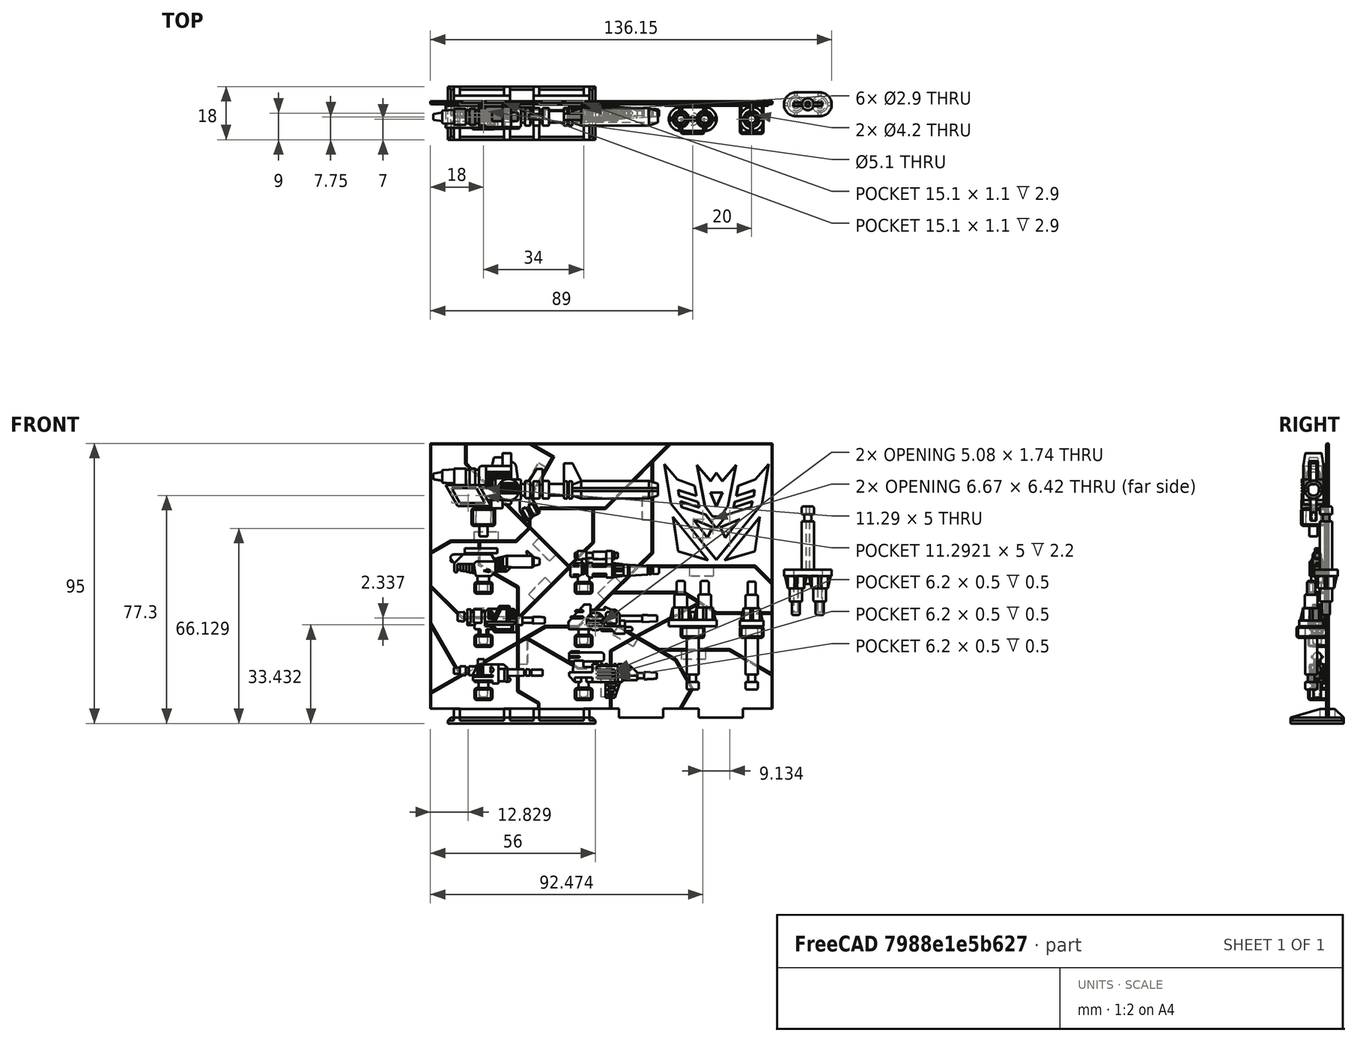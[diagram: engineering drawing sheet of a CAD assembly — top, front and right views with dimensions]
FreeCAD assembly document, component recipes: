
FREECAD ASSEMBLY — COMPONENT RECIPES ("Accesories")

This assembly document has 10 components, labeled P0..P9 below (a component is one placed body or linked part). 9 of them carry a construction recipe — the FreeCAD feature program that regenerates the part from scratch, quoted from this document or its linked companion documents; the rest are supplied as boundary geometry only. No exploded tour is included for this assembly.
NOTE — document 2 of 3 of this assembly tour. The two overview renders and the header above are repeated from document 1; the component sections below continue where the previous document stopped.
COMPONENT P4 — recipe-attached ("Scrapper_Gun", modeled in this document).
Construction recipe (the document's own serialized feature program — sketch geometry with constraints, then the solid features built on it; lengths are millimeters unless a unit is written):

FEATURE [Sketcher::SketchObject] Sketch283
  ArcFitTolerance = 1e-06
  AttachmentSupport = -> [XZ_Plane023]
  FullyConstrained = true
  MakeInternals = false
  MapMode = 5
  Placement = pos=(0,0,0) rot=(1,0,0;1.5708rad)
  sketch-geometry (15):
    g0: LineSegment StartX=0 StartY=0 StartZ=0 EndX=14.5 EndY=0 EndZ=0
    g1: LineSegment StartX=14.5 StartY=0 StartZ=0 EndX=16 EndY=-1.6 EndZ=0
    g2: LineSegment StartX=16 StartY=-1.6 StartZ=0 EndX=19.1 EndY=-1.6 EndZ=0
    g3: LineSegment StartX=19.1 StartY=-1.6 StartZ=0 EndX=19.1 EndY=2.9 EndZ=0
    g4: LineSegment StartX=19.1 StartY=2.9 StartZ=0 EndX=17.3 EndY=2.9 EndZ=0
    g5: LineSegment StartX=17.3 StartY=2.9 StartZ=0 EndX=17.3 EndY=5.2 EndZ=0
    g6: LineSegment StartX=17.3 StartY=5.2 StartZ=0 EndX=15.9 EndY=6.6 EndZ=0
    g7: LineSegment StartX=15.9 StartY=6.6 StartZ=0 EndX=14.4028 EndY=6.6 EndZ=0
    g8: LineSegment StartX=14.4028 StartY=6.6 StartZ=0 EndX=12.1028 EndY=7.6 EndZ=0
    g9: LineSegment StartX=12.1028 StartY=7.6 StartZ=0 EndX=12.1028 EndY=6.6 EndZ=0
    g10: LineSegment StartX=12.1028 StartY=6.6 StartZ=0 EndX=7.40278 EndY=6.6 EndZ=0
    g11: LineSegment StartX=7.40278 StartY=6.6 StartZ=0 EndX=7.40278 EndY=8.4 EndZ=0
    g12: LineSegment StartX=7.40278 StartY=8.4 StartZ=0 EndX=5.40278 EndY=8.4 EndZ=0
    g13: LineSegment StartX=5.40278 StartY=8.4 StartZ=0 EndX=0 EndY=2.5 EndZ=0
    g14: LineSegment StartX=0 StartY=2.5 StartZ=0 EndX=0 EndY=0 EndZ=0
  constraints (44):
    c: Coincident(g0,g-1)
    c: PointOnObject(g0,g-1)
    c: Coincident(g1,g0)
    c: Coincident(g2,g1)
    c: Horizontal(g2)
    c: Coincident(g3,g2)
    c: Vertical(g3)
    c: Coincident(g4,g3)
    c: Horizontal(g4)
    c: Coincident(g5,g4)
    c: Vertical(g5)
    c: Coincident(g6,g5)
    c: Coincident(g7,g6)
    c: Horizontal(g7)
    c: Coincident(g8,g7)
    c: Coincident(g9,g8)
    c: Coincident(g10,g9)
    c: Horizontal(g10)
    c: Coincident(g11,g10)
    c: Vertical(g11)
    c: Coincident(g12,g11)
    c: Horizontal(g12)
    c: Coincident(g13,g12)
    c: Coincident(g14,g13)
    c: Coincident(g14,g0)
    c: Vertical(g14)
    c: DistanceX(g0,g0) = 14.5
    c: DistanceY(g1,g0) = 1.6
    c: DistanceX(g2,g2) = 3.1
    c: DistanceY(g3,g3) = 4.5
    c: DistanceX(g0,g2) = 19.1
    c: DistanceX(g10,g10) = 4.7
    c: DistanceY(g14,g14) = 2.5
    c: DistanceY(g0,g12) = 8.4
    c: DistanceX(g12,g12) = 2
    c: DistanceX(g9,g7) = 2.3
    c: DistanceY(g11,g11) = 1.8
    c: Angle(g7,g6) = 2.35619
    c: DistanceX(g4,g4) = 1.8
    c: DistanceY(g7,g9) = 0
    c: Vertical(g9)
    c: Distance(g13) = 8
    c: DistanceY(g9,g9) = 1
    c: DistanceY(g5,g5) = 2.3
FEATURE [PartDesign::Pad] Pad188
  Direction = (0,-1,2e-16)
  Length = 4.5
  Length2 = 10
  Placement = pos=(0,0,0) rot=(1,0,0;1.5708rad)
  Profile = -> Sketch283
  ReferenceAxis = -> Sketch283 [N_Axis]
  Refine = true
  Suppressed = false
  Type = 0
FEATURE [Sketcher::SketchObject] Sketch284
  ArcFitTolerance = 1e-06
  AttachmentSupport = -> [Pad188]
  ExternalGeometry = -> [Pad188]
  FullyConstrained = true
  MakeInternals = false
  MapMode = 5
  Placement = pos=(0,-4.5,0) rot=(1,0,0;1.5708rad)
  sketch-geometry (1):
    g0: Circle CenterX=9.1 CenterY=2.6 CenterZ=0 NormalX=0 NormalY=0 NormalZ=1 AngleXU=0 Radius=3
  constraints (3):
    c: Diameter(g0) = 6
    c: DistanceX(g-1,g0) = 9.1
    c: DistanceY(g0,g-3) = 4
FEATURE [PartDesign::Pad] Pad189
  BaseFeature = -> Pad188
  Direction = (0,-1,2e-16)
  Length = 0.25
  Length2 = 10
  Placement = pos=(0,0,0) rot=(1,0,0;1.5708rad)
  Profile = -> Sketch284
  ReferenceAxis = -> Sketch284 [N_Axis]
  Refine = true
  Suppressed = false
  Type = 0
FEATURE [PartDesign::Pad] Pad190
  BaseFeature = -> Pad189
  Direction = (0,-1,2e-16)
  Length = 4.75
  Length2 = 10
  Placement = pos=(0,0,0) rot=(1,0,0;1.5708rad)
  Profile = -> Sketch284
  ReferenceAxis = -> Sketch284 [N_Axis]
  Refine = true
  Reversed = true
  Suppressed = false
  Type = 0
FEATURE [Sketcher::SketchObject] Sketch285
  ArcFitTolerance = 1e-06
  AttachmentSupport = -> [Pad190]
  ExternalGeometry = -> [Pad190]
  FullyConstrained = true
  MakeInternals = false
  MapMode = 5
  Placement = pos=(0,-4.5,0) rot=(1,0,0;1.5708rad)
  sketch-geometry (13):
    g0: LineSegment StartX=7.40278 StartY=6.6 StartZ=0 EndX=12.1028 EndY=6.6 EndZ=0
    g1: LineSegment StartX=12.1028 StartY=6.6 StartZ=0 EndX=12.1028 EndY=7.6 EndZ=0
    g2: LineSegment StartX=12.1028 StartY=7.6 StartZ=0 EndX=14.4028 EndY=6.6 EndZ=0
    g3: LineSegment StartX=14.4028 StartY=6.6 StartZ=0 EndX=15.9 EndY=6.6 EndZ=0
    g4: LineSegment StartX=15.9 StartY=6.6 StartZ=0 EndX=17.3 EndY=5.2 EndZ=0
    g5: LineSegment StartX=17.3 StartY=5.2 StartZ=0 EndX=17.3 EndY=2.9 EndZ=0
    g6: LineSegment StartX=17.3 StartY=2.9 StartZ=0 EndX=19.1 EndY=2.9 EndZ=0
    g7: LineSegment StartX=19.1 StartY=2.9 StartZ=0 EndX=19.1 EndY=-1.6 EndZ=0
    g8: LineSegment StartX=19.1 StartY=-1.6 StartZ=0 EndX=16 EndY=-1.6 EndZ=0
    g9: LineSegment StartX=16 StartY=-1.6 StartZ=0 EndX=14.5 EndY=0 EndZ=0
    g10: LineSegment StartX=14.5 StartY=0 StartZ=0 EndX=10.5967 EndY=6.8927e-12 EndZ=0
    g11: LineSegment StartX=7.40278 StartY=6.6 StartZ=0 EndX=7.40278 EndY=5.07375 EndZ=0
    g12: ArcOfCircle CenterX=9.10001 CenterY=2.6 CenterZ=0 NormalX=0 NormalY=0 NormalZ=1 AngleXU=0 Radius=3 StartAngle=5.2347 EndAngle=8.45532
  constraints (28):
    c: Coincident(g0,g-3)
    c: Coincident(g0,g-4)
    c: Coincident(g1,g0)
    c: Coincident(g1,g-5)
    c: Coincident(g2,g1)
    c: Coincident(g2,g-6)
    c: Coincident(g3,g2)
    c: Coincident(g3,g-7)
    c: Coincident(g4,g3)
    c: Coincident(g4,g-8)
    c: Coincident(g5,g4)
    c: Coincident(g5,g-9)
    c: Coincident(g6,g5)
    c: Coincident(g6,g-10)
    c: Coincident(g7,g6)
    c: Coincident(g7,g-11)
    c: Coincident(g8,g7)
    c: Coincident(g8,g-12)
    c: Coincident(g9,g8)
    c: Coincident(g9,g-13)
    c: Coincident(g10,g9)
    c: Coincident(g10,g-13)
    c: Coincident(g11,g0)
    c: PointOnObject(g11,g-14)
    c: Vertical(g11)
    c: Coincident(g12,g11)
    c: Coincident(g12,g10)
    c: Tangent(g12,g-14)
FEATURE [PartDesign::Pocket] Pocket046
  BaseFeature = -> Pad190
  Direction = (0,1,-2e-16)
  Length = 1
  Length2 = 5
  Placement = pos=(0,0,0) rot=(1,0,0;1.5708rad)
  Profile = -> Sketch285
  ReferenceAxis = -> Sketch285 [N_Axis]
  Refine = true
  Suppressed = false
  Type = 0
FEATURE [Sketcher::SketchObject] Sketch286
  ArcFitTolerance = 1e-06
  AttachmentSupport = -> [Pocket046]
  ExternalGeometry = -> [Pocket046]
  FullyConstrained = true
  MakeInternals = false
  MapMode = 5
  Placement = pos=(0,7e-16,0) rot=(-1,0,0;1.5708rad)
  sketch-geometry (13):
    g0: LineSegment StartX=7.40278 StartY=-6.6 StartZ=0 EndX=7.40278 EndY=-5.07375 EndZ=0
    g1: LineSegment StartX=7.40278 StartY=-6.6 StartZ=0 EndX=12.1028 EndY=-6.6 EndZ=0
    g2: LineSegment StartX=12.1028 StartY=-6.6 StartZ=0 EndX=12.1028 EndY=-7.6 EndZ=0
    g3: LineSegment StartX=12.1028 StartY=-7.6 StartZ=0 EndX=14.4028 EndY=-6.6 EndZ=0
    g4: LineSegment StartX=14.4028 StartY=-6.6 StartZ=0 EndX=15.9 EndY=-6.6 EndZ=0
    g5: LineSegment StartX=15.9 StartY=-6.6 StartZ=0 EndX=17.3 EndY=-5.2 EndZ=0
    g6: LineSegment StartX=17.3 StartY=-5.2 StartZ=0 EndX=17.3 EndY=-2.9 EndZ=0
    g7: LineSegment StartX=17.3 StartY=-2.9 StartZ=0 EndX=19.1 EndY=-2.9 EndZ=0
    g8: LineSegment StartX=19.1 StartY=-2.9 StartZ=0 EndX=19.1 EndY=1.6 EndZ=0
    g9: LineSegment StartX=19.1 StartY=1.6 StartZ=0 EndX=16 EndY=1.6 EndZ=0
    g10: LineSegment StartX=16 StartY=1.6 StartZ=0 EndX=14.5 EndY=0 EndZ=0
    g11: LineSegment StartX=14.5 StartY=0 StartZ=0 EndX=10.5967 EndY=0 EndZ=0
    g12: ArcOfCircle CenterX=9.1 CenterY=-2.6 CenterZ=0 NormalX=0 NormalY=0 NormalZ=1 AngleXU=0 Radius=3 StartAngle=4.11106 EndAngle=7.33167
  constraints (28):
    c: Coincident(g0,g-3)
    c: PointOnObject(g0,g-14)
    c: Vertical(g0)
    c: Coincident(g1,g0)
    c: Coincident(g1,g-4)
    c: Coincident(g2,g1)
    c: Coincident(g2,g-5)
    c: Coincident(g3,g2)
    c: Coincident(g3,g-6)
    c: Coincident(g4,g3)
    c: Coincident(g4,g-7)
    c: Coincident(g5,g4)
    c: Coincident(g5,g-8)
    c: Coincident(g6,g5)
    c: Coincident(g6,g-9)
    c: Coincident(g7,g6)
    c: Coincident(g7,g-10)
    c: Coincident(g8,g7)
    c: Coincident(g8,g-11)
    c: Coincident(g9,g8)
    c: Coincident(g9,g-12)
    c: Coincident(g10,g9)
    c: Coincident(g10,g-13)
    c: Coincident(g11,g10)
    c: Coincident(g11,g-13)
    c: Coincident(g12,g11)
    c: Coincident(g12,g0)
    c: Tangent(g12,g-14)
FEATURE [PartDesign::Pocket] Pocket047
  BaseFeature = -> Pocket046
  Direction = (0,-1,-2e-16)
  Length = 1
  Length2 = 5
  Placement = pos=(0,0,0) rot=(1,0,0;1.5708rad)
  Profile = -> Sketch286
  ReferenceAxis = -> Sketch286 [N_Axis]
  Refine = true
  Suppressed = false
  Type = 0
FEATURE [Sketcher::SketchObject] Sketch287
  ArcFitTolerance = 1e-06
  AttachmentSupport = -> [Pocket047]
  ExternalGeometry = -> [Pocket047]
  FullyConstrained = true
  MakeInternals = false
  MapMode = 5
  Placement = pos=(0,0,0) rot=(0.707107,0,-0.707107;3.14159rad)
  sketch-geometry (6):
    g0: LineSegment StartX=0 StartY=4.5 StartZ=0 EndX=-8.4 EndY=3.75 EndZ=0
    g1: LineSegment StartX=0 StartY=0 StartZ=0 EndX=-8.4 EndY=0.75 EndZ=0
    g2: LineSegment StartX=-8.4 StartY=3.75 StartZ=0 EndX=-8.4 EndY=4.5 EndZ=0
    g3: LineSegment StartX=-8.4 StartY=4.5 StartZ=0 EndX=0 EndY=4.5 EndZ=0
    g4: LineSegment StartX=-8.4 StartY=0.75 StartZ=0 EndX=-8.4 EndY=0 EndZ=0
    g5: LineSegment StartX=-8.4 StartY=0 StartZ=0 EndX=0 EndY=0 EndZ=0
  constraints (15):
    c: Coincident(g0,g-8)
    c: PointOnObject(g0,g-4)
    c: Coincident(g1,g-1)
    c: PointOnObject(g1,g-4)
    c: DistanceY(g1,g0) = 3
    c: DistanceY(g-5,g-4) = 4.5
    c: DistanceY(g-5,g1) = 0.75
    c: Coincident(g2,g0)
    c: Coincident(g2,g-4)
    c: Coincident(g3,g2)
    c: Coincident(g3,g0)
    c: Coincident(g4,g1)
    c: Coincident(g4,g-5)
    c: Coincident(g5,g4)
    c: Coincident(g5,g1)
FEATURE [PartDesign::Pocket] Pocket048
  BaseFeature = -> Pocket047
  Direction = (1,0,2e-16)
  Length = 8
  Length2 = 5
  Placement = pos=(0,0,0) rot=(1,0,0;1.5708rad)
  Profile = -> Sketch287
  ReferenceAxis = -> Sketch287 [N_Axis]
  Refine = true
  Suppressed = false
  Type = 0
FEATURE [Sketcher::SketchObject] Sketch288
  ArcFitTolerance = 1e-06
  AttachmentSupport = -> [Pocket048]
  ExternalGeometry = -> [Pocket048]
  FullyConstrained = true
  MakeInternals = false
  MapMode = 5
  Placement = pos=(0,0.25,0) rot=(-1,0,0;1.5708rad)
  sketch-geometry (1):
    g0: Circle CenterX=9.1 CenterY=-2.6 CenterZ=0 NormalX=0 NormalY=0 NormalZ=1 AngleXU=0 Radius=3
  constraints (2):
    c: Coincident(g0,g-3)
    c: Equal(g0,g-3)
FEATURE [PartDesign::Pad] Pad191
  BaseFeature = -> Pocket048
  Direction = (0,1,2e-16)
  Length = 5
  Length2 = 10
  Placement = pos=(0,0,0) rot=(1,0,0;1.5708rad)
  Profile = -> Sketch288
  ReferenceAxis = -> Sketch288 [N_Axis]
  Refine = true
  Reversed = true
  Suppressed = false
  Type = 0
FEATURE [Sketcher::SketchObject] Sketch289
  ArcFitTolerance = 1e-06
  AttachmentSupport = -> [Pad191]
  ExternalGeometry = -> [Pad191]
  FullyConstrained = true
  MakeInternals = false
  MapMode = 5
  Placement = pos=(0,-1,0) rot=(-1,0,0;1.5708rad)
  sketch-geometry (6):
    g0: LineSegment StartX=10.5967 StartY=-5.51634e-11 StartZ=0 EndX=14.5 EndY=2e-16 EndZ=0
    g1: LineSegment StartX=14.5 StartY=2e-16 StartZ=0 EndX=16 EndY=1.6 EndZ=0
    g2: LineSegment StartX=16 StartY=1.6 StartZ=0 EndX=19.1 EndY=1.6 EndZ=0
    g3: LineSegment StartX=19.1 StartY=1.6 StartZ=0 EndX=19.1 EndY=-1 EndZ=0
    g4: LineSegment StartX=19.1 StartY=-1 StartZ=0 EndX=11.6377 EndY=-1 EndZ=0
    g5: ArcOfCircle CenterX=9.10002 CenterY=-2.59998 CenterZ=0 NormalX=0 NormalY=0 NormalZ=1 AngleXU=0 Radius=2.99997 StartAngle=0.562534 EndAngle=1.04848
  constraints (15):
    c: Coincident(g0,g-3)
    c: Coincident(g0,g-5)
    c: Coincident(g1,g0)
    c: Coincident(g1,g-6)
    c: Coincident(g2,g1)
    c: Coincident(g2,g-7)
    c: Coincident(g3,g2)
    c: Coincident(g4,g3)
    c: PointOnObject(g4,g-4)
    c: Horizontal(g4)
    c: Coincident(g5,g4)
    c: Coincident(g5,g0)
    c: PointOnObject(g3,g-7)
    c: DistanceY(g3,g0) = 1
    c: Tangent(g-4,g5)
FEATURE [PartDesign::Pad] Pad192
  BaseFeature = -> Pad191
  Direction = (0,1,2e-16)
  Length = 0.6
  Length2 = 10
  Placement = pos=(0,0,0) rot=(1,0,0;1.5708rad)
  Profile = -> Sketch289
  ReferenceAxis = -> Sketch289 [N_Axis]
  Refine = true
  Suppressed = false
  Type = 0
FEATURE [Sketcher::SketchObject] Sketch290
  ArcFitTolerance = 1e-06
  AttachmentSupport = -> [Pad192]
  ExternalGeometry = -> [Pad192]
  FullyConstrained = true
  MakeInternals = false
  MapMode = 5
  Placement = pos=(0,-3.5,0) rot=(1,0,0;1.5708rad)
  sketch-geometry (6):
    g0: LineSegment StartX=10.5967 StartY=4.33529e-11 StartZ=0 EndX=14.5 EndY=-2e-16 EndZ=0
    g1: LineSegment StartX=14.5 StartY=-2e-16 StartZ=0 EndX=16 EndY=-1.6 EndZ=0
    g2: LineSegment StartX=16 StartY=-1.6 StartZ=0 EndX=19.1 EndY=-1.6 EndZ=0
    g3: LineSegment StartX=19.1 StartY=-1.6 StartZ=0 EndX=19.1 EndY=1 EndZ=0
    g4: LineSegment StartX=19.1 StartY=1 StartZ=0 EndX=11.6377 EndY=1 EndZ=0
    g5: ArcOfCircle CenterX=9.10003 CenterY=2.59998 CenterZ=0 NormalX=0 NormalY=0 NormalZ=1 AngleXU=0 Radius=2.99997 StartAngle=5.2347 EndAngle=5.72065
  constraints (15):
    c: Coincident(g0,g-7)
    c: Coincident(g0,g-6)
    c: Coincident(g1,g0)
    c: Coincident(g1,g-5)
    c: Coincident(g2,g1)
    c: Coincident(g2,g-4)
    c: Coincident(g3,g2)
    c: Coincident(g4,g3)
    c: PointOnObject(g4,g-7)
    c: Horizontal(g4)
    c: Coincident(g5,g4)
    c: Coincident(g5,g0)
    c: DistanceY(g0,g3) = 1
    c: PointOnObject(g3,g-3)
    c: Tangent(g5,g-7)
FEATURE [PartDesign::Pad] Pad193
  BaseFeature = -> Pad192
  Direction = (0,-1,2e-16)
  Length = 0.6
  Length2 = 10
  Placement = pos=(0,0,0) rot=(1,0,0;1.5708rad)
  Profile = -> Sketch290
  ReferenceAxis = -> Sketch290 [N_Axis]
  Refine = true
  Suppressed = false
  Type = 0
FEATURE [PartDesign::Fillet] Fillet030
  Base = -> Pad193 [Edge82,Edge32,Edge4,Edge85,Edge30,Edge31,Edge80,Edge79,Edge84]
  BaseFeature = -> Pad193
  Placement = pos=(0,0,0) rot=(1,0,0;1.5708rad)
  Radius = 0.25
  Refine = true
  SupportTransform = false
  Suppressed = false
  UseAllEdges = false
FEATURE [Sketcher::SketchObject] Sketch291
  ArcFitTolerance = 1e-06
  AttachmentSupport = -> [Fillet030]
  ExternalGeometry = -> [Fillet030]
  FullyConstrained = true
  MakeInternals = false
  MapMode = 5
  Placement = pos=(0,-3.5,0) rot=(1,0,0;1.5708rad)
  sketch-geometry (4):
    g0: LineSegment StartX=17.3 StartY=2.9 StartZ=0 EndX=17.3 EndY=1 EndZ=0
    g1: LineSegment StartX=17.3 StartY=1 StartZ=0 EndX=19.1 EndY=1 EndZ=0
    g2: LineSegment StartX=19.1 StartY=1 StartZ=0 EndX=19.1 EndY=2.9 EndZ=0
    g3: LineSegment StartX=19.1 StartY=2.9 StartZ=0 EndX=17.3 EndY=2.9 EndZ=0
  constraints (10):
    c: Coincident(g0,g1)
    c: Coincident(g1,g2)
    c: Coincident(g2,g3)
    c: Coincident(g3,g0)
    c: Vertical(g0)
    c: Vertical(g2)
    c: Horizontal(g1)
    c: Horizontal(g3)
    c: Coincident(g0,g-3)
    c: Coincident(g1,g-5)
FEATURE [PartDesign::Pocket] Pocket049
  BaseFeature = -> Fillet030
  Direction = (0,1,-2e-16)
  Length = 0.6
  Length2 = 5
  Placement = pos=(0,0,0) rot=(1,0,0;1.5708rad)
  Profile = -> Sketch291
  ReferenceAxis = -> Sketch291 [N_Axis]
  Refine = true
  Suppressed = false
  Type = 0
FEATURE [Sketcher::SketchObject] Sketch292
  ArcFitTolerance = 1e-06
  AttachmentSupport = -> [Pocket049]
  ExternalGeometry = -> [Pocket049]
  FullyConstrained = true
  MakeInternals = false
  MapMode = 5
  Placement = pos=(0,-1,0) rot=(-1,0,0;1.5708rad)
  sketch-geometry (4):
    g0: LineSegment StartX=17.3 StartY=-2.9 StartZ=0 EndX=19.1 EndY=-2.9 EndZ=0
    g1: LineSegment StartX=19.1 StartY=-2.9 StartZ=0 EndX=19.1 EndY=-1 EndZ=0
    g2: LineSegment StartX=19.1 StartY=-1 StartZ=0 EndX=17.3 EndY=-1 EndZ=0
    g3: LineSegment StartX=17.3 StartY=-1 StartZ=0 EndX=17.3 EndY=-2.9 EndZ=0
  constraints (10):
    c: Coincident(g0,g1)
    c: Coincident(g1,g2)
    c: Coincident(g2,g3)
    c: Coincident(g3,g0)
    c: Horizontal(g0)
    c: Horizontal(g2)
    c: Vertical(g1)
    c: Vertical(g3)
    c: Coincident(g0,g-5)
    c: Coincident(g1,g-4)
FEATURE [PartDesign::Pocket] Pocket050
  BaseFeature = -> Pocket049
  Direction = (0,-1,-2e-16)
  Length = 0.6
  Length2 = 5
  Placement = pos=(0,0,0) rot=(1,0,0;1.5708rad)
  Profile = -> Sketch292
  ReferenceAxis = -> Sketch292 [N_Axis]
  Refine = true
  Suppressed = false
  Type = 0
FEATURE [Sketcher::SketchObject] Sketch293
  ArcFitTolerance = 1e-06
  AttachmentSupport = -> [Pocket050]
  ExternalGeometry = -> [Pocket050]
  FullyConstrained = true
  MakeInternals = false
  MapMode = 5
  Placement = pos=(0,-1,0) rot=(-1,0,0;1.5708rad)
  sketch-geometry (12):
    g0: LineSegment StartX=16.3 StartY=-5.25 StartZ=0 EndX=16.3 EndY=-2.35 EndZ=0
    g1: LineSegment StartX=15.8 StartY=-1.85 StartZ=0 EndX=13.2 EndY=-1.85 EndZ=0
    g2: LineSegment StartX=12.7 StartY=-2.35 StartZ=0 EndX=12.7 EndY=-5.25 EndZ=0
    g3: LineSegment StartX=13.2 StartY=-5.75 StartZ=0 EndX=15.8 EndY=-5.75 EndZ=0
    g4: ArcOfCircle CenterX=13.2 CenterY=-2.35 CenterZ=0 NormalX=0 NormalY=0 NormalZ=1 AngleXU=0 Radius=0.5 StartAngle=1.5708 EndAngle=3.14159
    g5: GeomPoint [constr] X=12.7 Y=-1.85 Z=0
    g6: ArcOfCircle CenterX=13.2 CenterY=-5.25 CenterZ=0 NormalX=0 NormalY=0 NormalZ=1 AngleXU=0 Radius=0.5 StartAngle=3.14159 EndAngle=4.71239
    g7: GeomPoint [constr] X=12.7 Y=-5.75 Z=0
    g8: ArcOfCircle CenterX=15.8 CenterY=-5.25 CenterZ=0 NormalX=0 NormalY=0 NormalZ=1 AngleXU=0 Radius=0.5 StartAngle=4.71239 EndAngle=6.28319
    g9: GeomPoint [constr] X=16.3 Y=-5.75 Z=0
    g10: ArcOfCircle CenterX=15.8 CenterY=-2.35 CenterZ=0 NormalX=0 NormalY=0 NormalZ=1 AngleXU=0 Radius=0.5 StartAngle=1e-16 EndAngle=1.5708
    g11: GeomPoint [constr] X=16.3 Y=-1.85 Z=0
  constraints (29):
    c: Vertical(g0)
    c: Vertical(g2)
    c: Horizontal(g1)
    c: Horizontal(g3)
    c: PointOnObject(g5,g1)
    c: PointOnObject(g5,g2)
    c: Tangent(g1,g4) = -1.5708
    c: Tangent(g2,g4) = -1.5708
    c: PointOnObject(g7,g2)
    c: PointOnObject(g7,g3)
    c: Tangent(g2,g6) = -1.5708
    c: Tangent(g3,g6) = -1.5708
    c: PointOnObject(g9,g0)
    c: PointOnObject(g9,g3)
    c: Tangent(g0,g8) = -1.5708
    c: Tangent(g3,g8) = -1.5708
    c: PointOnObject(g11,g0)
    c: PointOnObject(g11,g1)
    c: Tangent(g0,g10) = -1.5708
    c: Tangent(g1,g10) = -1.5708
    c: Radius(g8) = 0.5
    c: Radius(g6) = 0.5
    c: Radius(g10) = 0.5
    c: Radius(g4) = 0.5
    c: DistanceX(g2,g0) = 3.6
    c: DistanceY(g3,g1) = 3.9
    c: DistanceY(g-3,g-5) = 5.6
    c: DistanceY(g-3,g3) = 0.85
    c: DistanceX(g0,g-5) = 1
FEATURE [PartDesign::Pad] Pad194
  BaseFeature = -> Pocket050
  Direction = (0,1,2e-16)
  Length = 1.25
  Length2 = 10
  Placement = pos=(0,0,0) rot=(1,0,0;1.5708rad)
  Profile = -> Sketch293
  ReferenceAxis = -> Sketch293 [N_Axis]
  Refine = true
  Suppressed = false
  Type = 0
FEATURE [PartDesign::Pad] Pad195
  BaseFeature = -> Pad194
  Direction = (0,1,2e-16)
  Length = 3.75
  Length2 = 10
  Placement = pos=(0,0,0) rot=(1,0,0;1.5708rad)
  Profile = -> Sketch293
  ReferenceAxis = -> Sketch293 [N_Axis]
  Refine = true
  Reversed = true
  Suppressed = false
  Type = 0
FEATURE [Sketcher::SketchObject] Sketch294
  ArcFitTolerance = 1e-06
  AttachmentSupport = -> [Pad195]
  ExternalGeometry = -> [Pad195]
  FullyConstrained = false
  MakeInternals = false
  MapMode = 5
  Placement = pos=(0,-4.75,0) rot=(1,0,0;1.5708rad)
  sketch-geometry (8):
    g0: ArcOfCircle CenterX=2.57858 CenterY=6.1 CenterZ=0 NormalX=0 NormalY=0 NormalZ=1 AngleXU=0 Radius=0.3 StartAngle=1.5708 EndAngle=4.71239
    g1: ArcOfCircle CenterX=4.67858 CenterY=6.1 CenterZ=0 NormalX=0 NormalY=0 NormalZ=1 AngleXU=0 Radius=0.3 StartAngle=4.71239 EndAngle=7.85398
    g2: LineSegment StartX=2.57858 StartY=6.4 StartZ=0 EndX=4.67858 EndY=6.4 EndZ=0
    g3: LineSegment StartX=2.57858 StartY=5.8 StartZ=0 EndX=4.67858 EndY=5.8 EndZ=0
    g4: ArcOfCircle CenterX=0.978584 CenterY=4 CenterZ=0 NormalX=0 NormalY=0 NormalZ=1 AngleXU=0 Radius=0.3 StartAngle=1.5708 EndAngle=4.71239
    g5: ArcOfCircle CenterX=4.67858 CenterY=4 CenterZ=0 NormalX=0 NormalY=0 NormalZ=1 AngleXU=0 Radius=0.3 StartAngle=4.71239 EndAngle=7.85398
    g6: LineSegment StartX=0.978584 StartY=4.3 StartZ=0 EndX=4.67858 EndY=4.3 EndZ=0
    g7: LineSegment StartX=0.978584 StartY=3.7 StartZ=0 EndX=4.67858 EndY=3.7 EndZ=0
  constraints (19):
    c: Tangent(g0,g2) = 1.5708
    c: Tangent(g0,g3) = -1.5708
    c: Tangent(g1,g2) = 1.5708
    c: Tangent(g1,g3) = -1.5708
    c: Equal(g0,g1)
    c: Horizontal(g2)
    c: Tangent(g4,g6) = 1.5708
    c: Tangent(g4,g7) = -1.5708
    c: Tangent(g5,g6) = 1.5708
    c: Tangent(g5,g7) = -1.5708
    c: Equal(g4,g5)
    c: Horizontal(g6)
    c: Diameter(g0) = 0.6
    c: Diameter(g4) = 0.6
    c: DistanceX(g0,g1) = 2.1
    c: DistanceX(g4,g5) = 3.7
    c: DistanceY(g1,g-4) = 2.3
    c: DistanceY(g5,g1) = 2.1
    c: DistanceX(g1,g5) = 0
FEATURE [PartDesign::Pad] Pad196
  BaseFeature = -> Pad195
  Direction = (0,-1,2e-16)
  Length = 5
  Length2 = 10
  Placement = pos=(0,0,0) rot=(1,0,0;1.5708rad)
  Profile = -> Sketch294
  ReferenceAxis = -> Sketch294 [N_Axis]
  Refine = true
  Reversed = true
  Suppressed = false
  Type = 0
FEATURE [Sketcher::SketchObject] Sketch295
  ArcFitTolerance = 1e-06
  AttachmentSupport = -> [Pad196]
  ExternalGeometry = -> [Pad196]
  FullyConstrained = true
  MakeInternals = false
  MapMode = 5
  Placement = pos=(19.1,-8.6e-15,-4.78e-14) rot=(0.707107,0,0.707107;3.14159rad)
  sketch-geometry (1):
    g0: Circle CenterX=0 CenterY=2.25 CenterZ=0 NormalX=0 NormalY=0 NormalZ=1 AngleXU=0 Radius=0.7
  constraints (4):
    c: Diameter(g0) = 1.4
    c: PointOnObject(g0,g-2)
    c: DistanceY(g-3,g-3) = 3.7
    c: DistanceY(g0,g-3) = 1.85
FEATURE [PartDesign::Pad] Pad197
  BaseFeature = -> Pad196
  Direction = (1,0,-2.4e-15)
  Length = 2.5
  Length2 = 10
  Placement = pos=(0,0,0) rot=(1,0,0;1.5708rad)
  Profile = -> Sketch295
  ReferenceAxis = -> Sketch295 [N_Axis]
  Refine = true
  Suppressed = false
  Type = 0
FEATURE [PartDesign::Pad] Pad198
  BaseFeature = -> Pad197
  Direction = (1,0,-2.4e-15)
  Length = 8.2
  Length2 = 10
  Placement = pos=(0,0,0) rot=(1,0,0;1.5708rad)
  Profile = -> Sketch295
  ReferenceAxis = -> Sketch295 [N_Axis]
  Refine = true
  Reversed = true
  Suppressed = false
  Type = 0
FEATURE [PartDesign::Fillet] Fillet031
  Base = -> Pad198 [Edge162,Edge223]
  BaseFeature = -> Pad198
  Placement = pos=(0,0,0) rot=(1,0,0;1.5708rad)
  Radius = 0.6
  Refine = true
  SupportTransform = false
  Suppressed = false
  UseAllEdges = false
FEATURE [Sketcher::SketchObject] Sketch296
  ArcFitTolerance = 1e-06
  AttachmentSupport = -> [Fillet031]
  ExternalGeometry = -> [Fillet031]
  FullyConstrained = true
  MakeInternals = false
  MapMode = 5
  Placement = pos=(0,0,0) rot=(1,0,0;3.14159rad)
  sketch-geometry (1):
    g0: Circle CenterX=5.10334 CenterY=2.25 CenterZ=0 NormalX=0 NormalY=0 NormalZ=1 AngleXU=0 Radius=1.7
  constraints (4):
    c: Radius(g0) = 1.7
    c: DistanceY(g-3,g-3) = 4.5
    c: DistanceY(g0,g-4) = 2.25
    c: DistanceX(g0,g-4) = 2.5
FEATURE [PartDesign::Pad] Pad199
  BaseFeature = -> Fillet031
  Direction = (0,0,-1)
  Length = 2
  Length2 = 10
  Placement = pos=(0,0,0) rot=(1,0,0;1.5708rad)
  Profile = -> Sketch296
  ReferenceAxis = -> Sketch296 [N_Axis]
  Refine = true
  Suppressed = false
  Type = 0
FEATURE [Sketcher::SketchObject] Sketch297
  ArcFitTolerance = 1e-06
  AttachmentSupport = -> [Pad199]
  ExternalGeometry = -> [Pad199]
  FullyConstrained = true
  MakeInternals = false
  MapMode = 5
  Placement = pos=(0,0,-2) rot=(1,0,0;3.14159rad)
  sketch-geometry (1):
    g0: Circle CenterX=5.10334 CenterY=2.25 CenterZ=0 NormalX=0 NormalY=0 NormalZ=1 AngleXU=0 Radius=1.4
  constraints (2):
    c: Coincident(g0,g-3)
    c: Radius(g0) = 1.4
FEATURE [PartDesign::Pad] Pad200
  BaseFeature = -> Pad199
  Direction = (0,0,-1)
  Length = 3.1
  Length2 = 10
  Placement = pos=(0,0,0) rot=(1,0,0;1.5708rad)
  Profile = -> Sketch297
  ReferenceAxis = -> Sketch297 [N_Axis]
  Refine = true
  Suppressed = false
  Type = 0
FEATURE [PartDesign::Fillet] Fillet032
  Base = -> Pad200 [Edge234]
  BaseFeature = -> Pad200
  Placement = pos=(0,0,0) rot=(1,0,0;1.5708rad)
  Radius = 1
  Refine = true
  SupportTransform = false
  Suppressed = false
  UseAllEdges = false
FEATURE [Sketcher::SketchObject] Sketch298
  ArcFitTolerance = 1e-06
  AttachmentSupport = -> [Fillet032]
  ExternalGeometry = -> [Fillet032]
  FullyConstrained = true
  MakeInternals = false
  MapMode = 5
  Placement = pos=(0,-4.75,0) rot=(1,0,0;1.5708rad)
  sketch-geometry (28):
    g0: ArcOfCircle CenterX=9.1 CenterY=2.6 CenterZ=0 NormalX=0 NormalY=0 NormalZ=1 AngleXU=0 Radius=2.6 StartAngle=2.28016 EndAngle=2.92844
    g1: ArcOfCircle CenterX=9.1 CenterY=2.6 CenterZ=0 NormalX=0 NormalY=0 NormalZ=1 AngleXU=0 Radius=2.6 StartAngle=0.213149 EndAngle=0.86143
    g2: ArcOfCircle CenterX=9.1 CenterY=2.6 CenterZ=0 NormalX=0 NormalY=0 NormalZ=1 AngleXU=0 Radius=2.6 StartAngle=3.35474 EndAngle=4.00302
    g3: ArcOfCircle CenterX=9.1 CenterY=2.6 CenterZ=0 NormalX=0 NormalY=0 NormalZ=1 AngleXU=0 Radius=2.6 StartAngle=5.42176 EndAngle=6.07004
    g4: LineSegment StartX=6.80884 StartY=2.3 StartZ=0 EndX=11.3912 EndY=2.3 EndZ=0
    g5: LineSegment StartX=6.80884 StartY=2.9 StartZ=0 EndX=11.3912 EndY=2.9 EndZ=0
    g6: LineSegment StartX=10.3997 StartY=4.49281 StartZ=0 EndX=10.1673 EndY=3.99435 EndZ=0
    g7: LineSegment StartX=9.94073 StartY=3.85 StartZ=0 EndX=8.25927 EndY=3.85 EndZ=0
    g8: LineSegment StartX=7.80025 StartY=4.49281 StartZ=0 EndX=8.03269 EndY=3.99435 EndZ=0
    g9: LineSegment StartX=7.80025 StartY=0.707185 StartZ=0 EndX=8.03269 EndY=1.20565 EndZ=0
    g10: LineSegment StartX=8.25927 StartY=1.35 StartZ=0 EndX=9.94073 EndY=1.35 EndZ=0
    g11: LineSegment StartX=10.1673 StartY=1.20565 StartZ=0 EndX=10.3997 EndY=0.707185 EndZ=0
    g12: ArcOfCircle CenterX=8.25927 CenterY=1.1 CenterZ=0 NormalX=0 NormalY=0 NormalZ=1 AngleXU=0 Radius=0.25 StartAngle=1.5708 EndAngle=2.70526
    g13: GeomPoint [constr] X=8.1 Y=1.35 Z=0
    g14: ArcOfCircle CenterX=9.94073 CenterY=1.1 CenterZ=0 NormalX=0 NormalY=0 NormalZ=1 AngleXU=0 Radius=0.25 StartAngle=0.436332 EndAngle=1.5708
    g15: GeomPoint [constr] X=10.1 Y=1.35 Z=0
    g16: ArcOfCircle CenterX=8.25927 CenterY=4.1 CenterZ=0 NormalX=0 NormalY=0 NormalZ=1 AngleXU=0 Radius=0.25 StartAngle=3.57792 EndAngle=4.71239
    g17: GeomPoint [constr] X=8.1 Y=3.85 Z=0
    g18: ArcOfCircle CenterX=9.94073 CenterY=4.1 CenterZ=0 NormalX=0 NormalY=0 NormalZ=1 AngleXU=0 Radius=0.25 StartAngle=4.71239 EndAngle=5.84685
    g19: GeomPoint [constr] X=10.1 Y=3.85 Z=0
    g20: ArcOfCircle CenterX=6.80884 CenterY=2.05 CenterZ=0 NormalX=0 NormalY=0 NormalZ=1 AngleXU=0 Radius=0.25 StartAngle=1.5708 EndAngle=3.14159
    g21: ArcOfCircle CenterX=11.3912 CenterY=2.05 CenterZ=0 NormalX=0 NormalY=0 NormalZ=1 AngleXU=0 Radius=0.25 StartAngle=1e-16 EndAngle=1.5708
    g22: ArcOfCircle CenterX=7.57374 CenterY=0.81299 CenterZ=0 NormalX=0 NormalY=0 NormalZ=1 AngleXU=0 Radius=0.25 StartAngle=3.97946 EndAngle=5.84619
    g23: ArcOfCircle CenterX=10.6263 CenterY=0.81299 CenterZ=0 NormalX=0 NormalY=0 NormalZ=1 AngleXU=0 Radius=0.25 StartAngle=3.57859 EndAngle=5.44531
    g24: ArcOfCircle CenterX=6.80884 CenterY=3.15 CenterZ=0 NormalX=0 NormalY=0 NormalZ=1 AngleXU=0 Radius=0.25 StartAngle=3.14159 EndAngle=4.71239
    g25: ArcOfCircle CenterX=11.3912 CenterY=3.15 CenterZ=0 NormalX=0 NormalY=0 NormalZ=1 AngleXU=0 Radius=0.25 StartAngle=4.71239 EndAngle=6.28319
    g26: ArcOfCircle CenterX=10.6263 CenterY=4.38701 CenterZ=0 NormalX=0 NormalY=0 NormalZ=1 AngleXU=0 Radius=0.25 StartAngle=0.837871 EndAngle=2.7046
    g27: ArcOfCircle CenterX=7.57374 CenterY=4.38701 CenterZ=0 NormalX=0 NormalY=0 NormalZ=1 AngleXU=0 Radius=0.25 StartAngle=0.436997 EndAngle=2.30372
  constraints (84):
    c: Horizontal(g4)
    c: Horizontal(g7)
    c: Horizontal(g10)
    c: Coincident(g0,g-3)
    c: Coincident(g1,g0)
    c: Coincident(g2,g0)
    c: Coincident(g3,g0)
    c: Horizontal(g5)
    c: Radius(g2) = 2.6
    c: Radius(g3) = 2.6
    c: Radius(g1) = 2.6
    c: Radius(g0) = 2.6
    c: DistanceY(g13,g2) = 0.7
    c: DistanceX(g17,g19) = 2
    c: DistanceX(g13,g15) = 2
    c: DistanceX(g17,g0) = 1
    c: DistanceX(g13,g0) = 1
    c: PointOnObject(g13,g9)
    c: PointOnObject(g13,g10)
    c: Tangent(g9,g12) = 1.5708
    c: Tangent(g10,g12) = 1.5708
    c: PointOnObject(g15,g10)
    c: PointOnObject(g15,g11)
    c: Tangent(g10,g14) = 1.5708
    c: Tangent(g11,g14) = 1.5708
    c: PointOnObject(g17,g7)
    c: PointOnObject(g17,g8)
    c: Tangent(g7,g16) = 1.5708
    c: Tangent(g8,g16) = -1.5708
    c: PointOnObject(g19,g6)
    c: PointOnObject(g19,g7)
    c: Tangent(g6,g18) = 1.5708
    c: Tangent(g7,g18) = 1.5708
    c: Coincident(g20,g4)
    c: Coincident(g20,g2)
    c: Coincident(g21,g4)
    c: Coincident(g21,g3)
    c: DistanceY(g4,g0) = 0.3
    c: DistanceX(g4,g20) = 0
    c: DistanceY(g2,g20) = 0
    c: DistanceX(g21,g4) = 0
    c: DistanceY(g3,g21) = 0
    c: Radius(g20) = 0.25
    c: Radius(g21) = 0.25
    c: Radius(g16) = 0.25
    c: Radius(g18) = 0.25
    c: Radius(g14) = 0.25
    c: Radius(g12) = 0.25
    c: Angle(g9,g10) = 2.00713
    c: Angle(g10,g11) = 2.00713
    c: Coincident(g22,g2)
    c: Coincident(g22,g9)
    c: Radius(g22) = 0.25
    c: Coincident(g23,g3)
    c: Coincident(g23,g11)
    c: Radius(g23) = 0.25
    c: Distance(g9) = 0.55
    c: DistanceY(g2,g9) = 0.08
    c: Distance(g11) = 0.55
    c: DistanceY(g3,g11) = 0.08
    c: Angle(g7,g8) = 2.00713
    c: Angle(g6,g7) = 2.00713
    c: DistanceY(g0,g5) = 0.3
    c: Distance(g6) = 0.55
    c: Distance(g8) = 0.55
    c: Coincident(g24,g5)
    c: Coincident(g24,g0)
    c: DistanceY(g0,g7) = 0.7
    c: Coincident(g25,g5)
    c: Coincident(g25,g1)
    c: Coincident(g26,g1)
    c: Coincident(g26,g6)
    c: Coincident(g27,g8)
    c: Coincident(g27,g0)
    c: Radius(g24) = 0.25
    c: Radius(g25) = 0.25
    c: Radius(g26) = 0.25
    c: Radius(g27) = 0.25
    c: DistanceX(g24,g5) = 0
    c: DistanceX(g5,g25) = 0
    c: DistanceY(g24,g0) = 0
    c: DistanceY(g25,g1) = 0
    c: DistanceY(g6,g1) = 0.08
    c: DistanceY(g8,g0) = 0.08
FEATURE [PartDesign::Pad] Pad201
  BaseFeature = -> Fillet032
  Direction = (0,-1,2e-16)
  Length = 0.3
  Length2 = 10
  Placement = pos=(0,0,0) rot=(1,0,0;1.5708rad)
  Profile = -> Sketch298
  ReferenceAxis = -> Sketch298 [N_Axis]
  Refine = true
  Suppressed = false
  Type = 0
FEATURE [PartDesign::Pad] Pad202
  BaseFeature = -> Pad201
  Direction = (0,-1,2e-16)
  Length = 5.3
  Length2 = 10
  Placement = pos=(0,0,0) rot=(1,0,0;1.5708rad)
  Profile = -> Sketch298
  ReferenceAxis = -> Sketch298 [N_Axis]
  Refine = true
  Reversed = true
  Suppressed = false
  Type = 0
FEATURE [PartDesign::Fillet] Fillet033
  Base = -> Pad202 [Edge247,Edge245,Edge243,Edge264,Edge263,Edge261,Edge259,Edge249,Edge251,Edge253,Edge255,Edge257,Edge219,Edge240,Edge239,Edge237,Edge235,Edge231,Edge233,Edge229,Edge227,Edge225,Edge223,Edge221,Edge319,Edge307,Edge313,Edge311,Edge315,Edge317,Edge310,Edge303,Edge306,Edge325,Edge323,Edge321,Edge291,Edge290,Edge287,Edge285,+8 more]
  BaseFeature = -> Pad202
  Placement = pos=(0,0,0) rot=(1,0,0;1.5708rad)
  Radius = 0.2
  Refine = true
  SupportTransform = false
  Suppressed = false
  UseAllEdges = false
FEATURE [Sketcher::SketchObject] Sketch299
  ArcFitTolerance = 1e-06
  AttachmentSupport = -> [Fillet033]
  ExternalGeometry = -> [Fillet033]
  FullyConstrained = true
  MakeInternals = false
  MapMode = 5
  Placement = pos=(17.3,-2.92e-14,-8.68e-14) rot=(0.707107,0,0.707107;3.14159rad)
  sketch-geometry (1):
    g0: Circle CenterX=3.59282 CenterY=2.25 CenterZ=0 NormalX=0 NormalY=0 NormalZ=1 AngleXU=0 Radius=0.95
  constraints (4):
    c: Diameter(g0) = 1.9
    c: DistanceY(g-3,g-3) = 2.5
    c: DistanceY(g0,g-3) = 1.25
    c: PointOnObject(g-4,g0)
FEATURE [PartDesign::Pad] Pad203
  BaseFeature = -> Fillet033
  Direction = (1,-1.7e-15,-5.2e-15)
  Length = 7.7
  Length2 = 10
  Placement = pos=(0,0,0) rot=(1,0,0;1.5708rad)
  Profile = -> Sketch299
  ReferenceAxis = -> Sketch299 [N_Axis]
  Refine = true
  Suppressed = false
  Type = 0
FEATURE [Sketcher::SketchObject] Sketch300
  ArcFitTolerance = 1e-06
  AttachmentSupport = -> [Pad203]
  ExternalGeometry = -> [Pad203]
  FullyConstrained = true
  MakeInternals = false
  MapMode = 5
  Placement = pos=(25,-5.4e-14,-1.558e-13) rot=(0.707107,0,0.707107;3.14159rad)
  sketch-geometry (1):
    g0: Circle CenterX=3.59282 CenterY=2.25 CenterZ=0 NormalX=0 NormalY=0 NormalZ=1 AngleXU=0 Radius=1.2
  constraints (2):
    c: Coincident(g0,g-3)
    c: Diameter(g0) = 2.4
FEATURE [Sketcher::SketchObject] Sketch301
  ArcFitTolerance = 1e-06
  AttachmentOffset = pos=(0,0,5) rot=(0,0,1;0rad)
  AttachmentSupport = -> [Pad203]
  ExternalGeometry = -> [Pad203]
  FullyConstrained = true
  MakeInternals = false
  MapMode = 5
  Placement = pos=(30,-6.48e-14,-1.86e-13) rot=(0.707107,0,0.707107;3.14159rad)
  sketch-geometry (1):
    g0: Circle CenterX=3.59282 CenterY=2.25 CenterZ=0 NormalX=0 NormalY=0 NormalZ=1 AngleXU=0 Radius=1
  constraints (2):
    c: Coincident(g0,g-3)
    c: Diameter(g0) = 2
FEATURE [PartDesign::Body] Body021  label="Scrapper_Gun"
  AllowCompound = false
  Group = -> [Sketch283,Pad188,Sketch284,Pad189,Pad190,Sketch285,Pocket046,Sketch286,Pocket047,Sketch287,Pocket048,Sketch288,Pad191,Sketch289,Pad192,Sketch290,Pad193,Fillet030,Sketch291,Pocket049,Sketch292,Pocket050,Sketch293,Pad194,Pad195,Sketch294,Pad196,Sketch295,Pad197,Pad198,Fillet031,Sketch296,Pad199,Sketch297,Pad200,Fillet032,Sketch298,Pad201,Pad202,Fillet033,Sketch299,Pad203,Sketch300,Sketch301,+3 more]
  Origin = -> Origin023
  Placement = pos=(-11.1,-0.75,-18) rot=(0,0,1;0rad)
  Tip = -> Fillet035
COMPONENT P5 — recipe-attached ("Mixmaster_Dual_Head_Missile", modeled in this document).
Construction recipe (the document's own serialized feature program — sketch geometry with constraints, then the solid features built on it; lengths are millimeters unless a unit is written):

FEATURE [Sketcher::SketchObject] Sketch302
  ArcFitTolerance = 1e-06
  AttachmentOffset = pos=(66,0,0) rot=(0,0,1;0rad)
  AttachmentSupport = -> [XY_Plane024]
  FullyConstrained = true
  MakeInternals = false
  MapMode = 5
  Placement = pos=(66,0,0) rot=(0,0,1;0rad)
  sketch-geometry (4):
    g0: ArcOfCircle CenterX=0 CenterY=0 CenterZ=0 NormalX=0 NormalY=0 NormalZ=1 AngleXU=0 Radius=4.05 StartAngle=1.5708 EndAngle=4.71239
    g1: ArcOfCircle CenterX=8.1 CenterY=-3e-16 CenterZ=0 NormalX=0 NormalY=0 NormalZ=1 AngleXU=0 Radius=4.05 StartAngle=4.71239 EndAngle=7.85398
    g2: LineSegment StartX=-7e-16 StartY=4.05 StartZ=0 EndX=8.1 EndY=4.05 EndZ=0
    g3: LineSegment StartX=-7e-16 StartY=-4.05 StartZ=0 EndX=8.1 EndY=-4.05 EndZ=0
  constraints (9):
    c: Tangent(g0,g2) = 1.5708
    c: Tangent(g0,g3) = -1.5708
    c: Tangent(g1,g2) = 1.5708
    c: Tangent(g1,g3) = -1.5708
    c: Equal(g0,g1)
    c: Coincident(g0,g-1)
    c: Horizontal(g2)
    c: Radius(g1) = 4.05
    c: DistanceX(g2,g2) = 8.1
FEATURE [PartDesign::Pad] Pad204
  Direction = (0,0,1)
  Length = 2.1
  Length2 = 10
  Profile = -> Sketch302
  ReferenceAxis = -> Sketch302 [N_Axis]
  Refine = true
  Suppressed = false
  Type = 0
FEATURE [Sketcher::SketchObject] Sketch303
  ArcFitTolerance = 1e-06
  AttachmentSupport = -> [Pad204]
  ExternalGeometry = -> [Pad204]
  FullyConstrained = true
  MakeInternals = false
  MapMode = 5
  Placement = pos=(0,0,2.1) rot=(0,0,1;0rad)
  sketch-geometry (1):
    g0: Circle CenterX=70.05 CenterY=0 CenterZ=0 NormalX=0 NormalY=0 NormalZ=1 AngleXU=0 Radius=2.05
  constraints (4):
    c: PointOnObject(g0,g-1)
    c: Radius(g0) = 2.05
    c: DistanceX(g-3,g-3) = 8.1
    c: DistanceX(g-3,g0) = 4.05
FEATURE [PartDesign::Pad] Pad205
  BaseFeature = -> Pad204
  Direction = (0,0,1)
  Length = 16.4
  Length2 = 10
  Profile = -> Sketch303
  ReferenceAxis = -> Sketch303 [N_Axis]
  Refine = true
  Suppressed = false
  Type = 0
FEATURE [Sketcher::SketchObject] Sketch304
  ArcFitTolerance = 1e-06
  AttachmentSupport = -> [Pad205]
  ExternalGeometry = -> [Pad205]
  FullyConstrained = true
  MakeInternals = false
  MapMode = 5
  Placement = pos=(0,0,18.5) rot=(0,0,1;0rad)
  sketch-geometry (1):
    g0: Circle CenterX=70.05 CenterY=0 CenterZ=0 NormalX=0 NormalY=0 NormalZ=1 AngleXU=0 Radius=1.15
  constraints (2):
    c: Coincident(g0,g-3)
    c: Radius(g0) = 1.15
FEATURE [PartDesign::Pad] Pad206
  BaseFeature = -> Pad205
  Direction = (0,0,1)
  Length = 2.5
  Length2 = 10
  Profile = -> Sketch304
  ReferenceAxis = -> Sketch304 [N_Axis]
  Refine = true
  Suppressed = false
  Type = 0
FEATURE [Sketcher::SketchObject] Sketch305
  ArcFitTolerance = 1e-06
  AttachmentSupport = -> [Pad206]
  ExternalGeometry = -> [Pad206]
  FullyConstrained = true
  MakeInternals = false
  MapMode = 5
  Placement = pos=(0,0,21) rot=(0,0,1;0rad)
  sketch-geometry (1):
    g0: Circle CenterX=70.05 CenterY=0 CenterZ=0 NormalX=0 NormalY=0 NormalZ=1 AngleXU=0 Radius=2.05
  constraints (2):
    c: Coincident(g0,g-3)
    c: Radius(g0) = 2.05
FEATURE [PartDesign::Pad] Pad207
  BaseFeature = -> Pad206
  Direction = (0,0,1)
  Length = 2.6
  Length2 = 10
  Profile = -> Sketch305
  ReferenceAxis = -> Sketch305 [N_Axis]
  Refine = true
  Suppressed = false
  Type = 0
FEATURE [PartDesign::Fillet] Fillet036
  Base = -> Pad207 [Edge21]
  BaseFeature = -> Pad207
  Radius = 0.5
  Refine = true
  SupportTransform = false
  Suppressed = false
  UseAllEdges = false
FEATURE [PartDesign::Fillet] Fillet037
  Base = -> Fillet036 [Edge22,Edge23,Edge20,Edge18]
  BaseFeature = -> Fillet036
  Radius = 0.2
  Refine = true
  SupportTransform = false
  Suppressed = false
  UseAllEdges = false
FEATURE [Sketcher::SketchObject] Sketch306
  ArcFitTolerance = 1e-06
  AttachmentSupport = -> [Fillet037]
  ExternalGeometry = -> [Fillet037]
  FullyConstrained = true
  MakeInternals = false
  MapMode = 5
  Placement = pos=(0,0,0) rot=(1,0,0;3.14159rad)
  sketch-geometry (2):
    g0: Circle CenterX=66 CenterY=0 CenterZ=0 NormalX=0 NormalY=0 NormalZ=1 AngleXU=0 Radius=2.75
    g1: Circle CenterX=74.1 CenterY=0 CenterZ=0 NormalX=0 NormalY=0 NormalZ=1 AngleXU=0 Radius=2.75
  constraints (4):
    c: Coincident(g0,g-4)
    c: Radius(g0) = 2.75
    c: Coincident(g1,g-3)
    c: Radius(g1) = 2.75
FEATURE [PartDesign::Pad] Pad208
  BaseFeature = -> Fillet037
  Direction = (0,0,-1)
  Length = 4.2
  Length2 = 10
  Profile = -> Sketch306
  ReferenceAxis = -> Sketch306 [N_Axis]
  Refine = true
  Suppressed = false
  Type = 0
FEATURE [Sketcher::SketchObject] Sketch307
  ArcFitTolerance = 1e-06
  AttachmentSupport = -> [Pad208]
  ExternalGeometry = -> [Pad208]
  FullyConstrained = false
  MakeInternals = false
  MapMode = 5
  Placement = pos=(0,0,0) rot=(1,0,0;3.14159rad)
  sketch-geometry (8):
    g0: ArcOfCircle CenterX=66 CenterY=5.36e-14 CenterZ=0 NormalX=0 NormalY=0 NormalZ=1 AngleXU=0 Radius=2.75 StartAngle=1.38796 EndAngle=1.75363
    g1: LineSegment StartX=65.5 StartY=2.70416 StartZ=0 EndX=65.5 EndY=3.70416 EndZ=0
    g2: LineSegment StartX=65.5 StartY=3.70416 StartZ=0 EndX=66.5 EndY=3.70416 EndZ=0
    g3: LineSegment StartX=66.5 StartY=3.70416 StartZ=0 EndX=66.5 EndY=2.70416 EndZ=0
    g4: ArcOfCircle CenterX=74.1 CenterY=-1.29e-14 CenterZ=0 NormalX=0 NormalY=0 NormalZ=1 AngleXU=0 Radius=2.75 StartAngle=1.38796 EndAngle=1.75363
    g5: LineSegment StartX=73.6 StartY=2.70416 StartZ=0 EndX=73.6 EndY=3.70416 EndZ=0
    g6: LineSegment StartX=73.6 StartY=3.70416 StartZ=0 EndX=74.6 EndY=3.70416 EndZ=0
    g7: LineSegment StartX=74.6 StartY=3.70416 StartZ=0 EndX=74.6 EndY=2.70416 EndZ=0
  constraints (22):
    c: Tangent(g0,g-3) = -1.5708
    c: PointOnObject(g0,g-3)
    c: Coincident(g1,g0)
    c: Vertical(g1)
    c: Coincident(g2,g1)
    c: Horizontal(g2)
    c: Coincident(g3,g2)
    c: Coincident(g3,g0)
    c: Vertical(g3)
    c: DistanceX(g2,g2) = 1
    c: DistanceY(g1,g1) = 1
    c: Tangent(g4,g-4) = -1.5708
    c: PointOnObject(g4,g-4)
    c: Coincident(g5,g4)
    c: Vertical(g5)
    c: Coincident(g6,g5)
    c: Horizontal(g6)
    c: Coincident(g7,g6)
    c: Coincident(g7,g4)
    c: DistanceX(g6,g6) = 1
    c: Vertical(g7)
    c: DistanceY(g7,g7) = 1
FEATURE [Sketcher::SketchObject] Sketch308
  ArcFitTolerance = 1e-06
  AttachmentSupport = -> [Pad208]
  ExternalGeometry = -> [Pad208,Sketch307]
  FullyConstrained = false
  MakeInternals = false
  MapMode = 5
  Placement = pos=(0,0,-4.2) rot=(1,0,0;3.14159rad)
  sketch-geometry (8):
    g0: ArcOfCircle CenterX=66 CenterY=3.61e-14 CenterZ=0 NormalX=0 NormalY=0 NormalZ=1 AngleXU=0 Radius=2.75 StartAngle=1.38796 EndAngle=1.75363
    g1: LineSegment StartX=65.5 StartY=2.70416 StartZ=0 EndX=65.5 EndY=2.75 EndZ=0
    g2: LineSegment StartX=66.5 StartY=2.70416 StartZ=0 EndX=66.5 EndY=2.75 EndZ=0
    g3: LineSegment StartX=65.5 StartY=2.75 StartZ=0 EndX=66.5 EndY=2.75 EndZ=0
    g4: ArcOfCircle CenterX=74.1 CenterY=3.96866e-06 CenterZ=0 NormalX=0 NormalY=0 NormalZ=1 AngleXU=0 Radius=2.75 StartAngle=1.38796 EndAngle=1.75363
    g5: LineSegment StartX=73.6 StartY=2.70416 StartZ=0 EndX=73.6 EndY=2.75 EndZ=0
    g6: LineSegment StartX=74.6 StartY=2.70416 StartZ=0 EndX=74.6 EndY=2.75 EndZ=0
    g7: LineSegment StartX=74.6 StartY=2.75 StartZ=0 EndX=73.6 EndY=2.75 EndZ=0
  constraints (21):
    c: Coincident(g0,g-7)
    c: Coincident(g0,g-6)
    c: Coincident(g1,g0)
    c: PointOnObject(g1,g-7)
    c: Coincident(g2,g0)
    c: PointOnObject(g2,g-6)
    c: Coincident(g3,g1)
    c: Coincident(g3,g2)
    c: Horizontal(g3)
    c: Tangent(g3,g0)
    c: Coincident(g4,g-18)
    c: Coincident(g4,g-19)
    c: Tangent(g4,g-20)
    c: Coincident(g5,g4)
    c: PointOnObject(g5,g-19)
    c: Coincident(g6,g4)
    c: PointOnObject(g6,g-18)
    c: Coincident(g7,g6)
    c: Coincident(g7,g5)
    c: Horizontal(g7)
    c: Tangent(g7,g4)
FEATURE [PartDesign::AdditiveLoft] AdditiveLoft012
  BaseFeature = -> Pad208
  Closed = false
  Profile = -> Sketch307
  Refine = true
  Ruled = false
  Sections = -> [Sketch308]
  Suppressed = false
FEATURE [Sketcher::SketchObject] Sketch309
  ArcFitTolerance = 1e-06
  AttachmentSupport = -> [AdditiveLoft012]
  ExternalGeometry = -> [AdditiveLoft012]
  FullyConstrained = true
  MakeInternals = false
  MapMode = 5
  Placement = pos=(0,0,0) rot=(1,0,0;3.14159rad)
  sketch-geometry (8):
    g0: ArcOfCircle CenterX=66 CenterY=0 CenterZ=0 NormalX=0 NormalY=0 NormalZ=1 AngleXU=0 Radius=2.75 StartAngle=6.10035 EndAngle=6.46602
    g1: LineSegment StartX=68.7042 StartY=0.5 StartZ=0 EndX=69.7042 EndY=0.5 EndZ=0
    g2: LineSegment StartX=69.7042 StartY=0.5 StartZ=0 EndX=69.7042 EndY=-0.5 EndZ=0
    g3: LineSegment StartX=69.7042 StartY=-0.5 StartZ=0 EndX=68.7042 EndY=-0.5 EndZ=0
    g4: ArcOfCircle CenterX=74.1 CenterY=0 CenterZ=0 NormalX=0 NormalY=0 NormalZ=1 AngleXU=0 Radius=2.75 StartAngle=6.10035 EndAngle=6.46602
    g5: LineSegment StartX=76.8042 StartY=0.5 StartZ=0 EndX=77.8042 EndY=0.5 EndZ=0
    g6: LineSegment StartX=77.8042 StartY=0.5 StartZ=0 EndX=77.8042 EndY=-0.5 EndZ=0
    g7: LineSegment StartX=77.8042 StartY=-0.5 StartZ=0 EndX=76.8042 EndY=-0.5 EndZ=0
  constraints (24):
    c: Coincident(g1,g0)
    c: Horizontal(g1)
    c: Coincident(g2,g1)
    c: Vertical(g2)
    c: Coincident(g3,g2)
    c: Coincident(g3,g0)
    c: Horizontal(g3)
    c: DistanceX(g1,g1) = 1
    c: DistanceY(g2,g2) = 1
    c: DistanceY(g0,g0) = 0.5
    c: Coincident(g0,g-4)
    c: PointOnObject(g-4,g0)
    c: PointOnObject(g4,g-5)
    c: Coincident(g4,g-6)
    c: Coincident(g5,g4)
    c: Coincident(g6,g5)
    c: Vertical(g6)
    c: Coincident(g7,g6)
    c: Coincident(g7,g4)
    c: Horizontal(g5)
    c: Horizontal(g7)
    c: DistanceY(g6,g6) = 1
    c: DistanceX(g5,g5) = 1
    c: DistanceY(g4,g5) = 0.5
FEATURE [Sketcher::SketchObject] Sketch310
  ArcFitTolerance = 1e-06
  AttachmentSupport = -> [AdditiveLoft012]
  ExternalGeometry = -> [AdditiveLoft012,Sketch309]
  FullyConstrained = true
  MakeInternals = false
  MapMode = 5
  Placement = pos=(0,0,-4.2) rot=(1,0,0;3.14159rad)
  sketch-geometry (8):
    g0: ArcOfCircle CenterX=66 CenterY=1.1e-15 CenterZ=0 NormalX=0 NormalY=0 NormalZ=1 AngleXU=0 Radius=2.75001 StartAngle=6.10035 EndAngle=6.46602
    g1: ArcOfCircle CenterX=74.1 CenterY=-4e-15 CenterZ=0 NormalX=0 NormalY=0 NormalZ=1 AngleXU=0 Radius=2.75001 StartAngle=6.10035 EndAngle=6.46602
    g2: LineSegment StartX=68.7042 StartY=0.5 StartZ=0 EndX=68.75 EndY=0.5 EndZ=0
    g3: LineSegment StartX=68.7042 StartY=-0.5 StartZ=0 EndX=68.75 EndY=-0.5 EndZ=0
    g4: LineSegment StartX=68.75 StartY=0.5 StartZ=0 EndX=68.75 EndY=-0.5 EndZ=0
    g5: LineSegment StartX=76.8042 StartY=0.5 StartZ=0 EndX=76.85 EndY=0.5 EndZ=0
    g6: LineSegment StartX=76.8042 StartY=-0.5 StartZ=0 EndX=76.85 EndY=-0.5 EndZ=0
    g7: LineSegment StartX=76.85 StartY=0.5 StartZ=0 EndX=76.85 EndY=-0.5 EndZ=0
  constraints (22):
    c: Coincident(g0,g-7)
    c: Coincident(g0,g-8)
    c: Coincident(g1,g-9)
    c: Coincident(g1,g-10)
    c: Tangent(g0,g-5)
    c: Tangent(g1,g-4)
    c: Coincident(g2,g0)
    c: PointOnObject(g2,g-7)
    c: Coincident(g3,g0)
    c: PointOnObject(g3,g-8)
    c: Coincident(g4,g2)
    c: Coincident(g4,g3)
    c: Vertical(g4)
    c: Tangent(g4,g0)
    c: Coincident(g5,g1)
    c: PointOnObject(g5,g-9)
    c: Coincident(g6,g1)
    c: PointOnObject(g6,g-10)
    c: Coincident(g7,g5)
    c: Coincident(g7,g6)
    c: Vertical(g7)
    c: Tangent(g7,g1)
FEATURE [PartDesign::AdditiveLoft] AdditiveLoft013
  BaseFeature = -> AdditiveLoft012
  Closed = false
  Profile = -> Sketch309
  Refine = true
  Ruled = false
  Sections = -> [Sketch310]
  Suppressed = false
FEATURE [Sketcher::SketchObject] Sketch311
  ArcFitTolerance = 1e-06
  AttachmentSupport = -> [AdditiveLoft013]
  ExternalGeometry = -> [AdditiveLoft013]
  FullyConstrained = true
  MakeInternals = false
  MapMode = 5
  Placement = pos=(0,0,0) rot=(1,0,0;3.14159rad)
  sketch-geometry (8):
    g0: ArcOfCircle CenterX=66 CenterY=-4.6e-15 CenterZ=0 NormalX=0 NormalY=0 NormalZ=1 AngleXU=0 Radius=2.75 StartAngle=2.95876 EndAngle=3.32443
    g1: ArcOfCircle CenterX=74.1 CenterY=-3.7e-15 CenterZ=0 NormalX=0 NormalY=0 NormalZ=1 AngleXU=0 Radius=2.75 StartAngle=2.95876 EndAngle=3.32443
    g2: LineSegment StartX=71.3958 StartY=0.5 StartZ=0 EndX=70.3958 EndY=0.5 EndZ=0
    g3: LineSegment StartX=70.3958 StartY=0.5 StartZ=0 EndX=70.3958 EndY=-0.5 EndZ=0
    g4: LineSegment StartX=70.3958 StartY=-0.5 StartZ=0 EndX=71.3958 EndY=-0.5 EndZ=0
    g5: LineSegment StartX=63.2958 StartY=0.5 StartZ=0 EndX=62.2958 EndY=0.5 EndZ=0
    g6: LineSegment StartX=62.2958 StartY=0.5 StartZ=0 EndX=62.2958 EndY=-0.5 EndZ=0
    g7: LineSegment StartX=62.2958 StartY=-0.5 StartZ=0 EndX=63.2958 EndY=-0.5 EndZ=0
  constraints (24):
    c: Tangent(g0,g-4) = -1.5708
    c: PointOnObject(g0,g-4)
    c: Tangent(g1,g-3) = -1.5708
    c: PointOnObject(g1,g-3)
    c: Coincident(g2,g1)
    c: Horizontal(g2)
    c: Coincident(g3,g2)
    c: Vertical(g3)
    c: Coincident(g4,g3)
    c: Coincident(g4,g1)
    c: Horizontal(g4)
    c: Coincident(g5,g0)
    c: Horizontal(g5)
    c: Coincident(g6,g5)
    c: Vertical(g6)
    c: Coincident(g7,g6)
    c: Coincident(g7,g0)
    c: Horizontal(g7)
    c: DistanceX(g5,g5) = 1
    c: DistanceX(g2,g2) = 1
    c: DistanceY(g3,g3) = 1
    c: DistanceY(g6,g6) = 1
    c: DistanceY(g0,g0) = 0.5
    c: DistanceY(g1,g1) = 0.5
FEATURE [Sketcher::SketchObject] Sketch312
  ArcFitTolerance = 1e-06
  AttachmentSupport = -> [AdditiveLoft013]
  ExternalGeometry = -> [AdditiveLoft013,Sketch311]
  FullyConstrained = true
  MakeInternals = false
  MapMode = 5
  Placement = pos=(0,0,-4.2) rot=(1,0,0;3.14159rad)
  sketch-geometry (8):
    g0: ArcOfCircle CenterX=66 CenterY=3.6e-15 CenterZ=0 NormalX=0 NormalY=0 NormalZ=1 AngleXU=0 Radius=2.74997 StartAngle=2.95876 EndAngle=3.32443
    g1: ArcOfCircle CenterX=74.1 CenterY=-3.94e-14 CenterZ=0 NormalX=0 NormalY=0 NormalZ=1 AngleXU=0 Radius=2.75 StartAngle=2.95876 EndAngle=3.32443
    g2: LineSegment StartX=63.2958 StartY=0.5 StartZ=0 EndX=63.25 EndY=0.5 EndZ=0
    g3: LineSegment StartX=63.25 StartY=0.5 StartZ=0 EndX=63.25 EndY=-0.5 EndZ=0
    g4: LineSegment StartX=63.25 StartY=-0.5 StartZ=0 EndX=63.2958 EndY=-0.5 EndZ=0
    g5: LineSegment StartX=71.3958 StartY=0.5 StartZ=0 EndX=71.35 EndY=0.5 EndZ=0
    g6: LineSegment StartX=71.35 StartY=0.5 StartZ=0 EndX=71.35 EndY=-0.5 EndZ=0
    g7: LineSegment StartX=71.35 StartY=-0.5 StartZ=0 EndX=71.3958 EndY=-0.5 EndZ=0
  constraints (22):
    c: Coincident(g0,g-5)
    c: Coincident(g0,g-6)
    c: Coincident(g1,g-7)
    c: Coincident(g1,g-8)
    c: Coincident(g2,g0)
    c: PointOnObject(g2,g-5)
    c: Coincident(g3,g2)
    c: PointOnObject(g3,g-6)
    c: Vertical(g3)
    c: Coincident(g4,g3)
    c: Coincident(g4,g0)
    c: Tangent(g0,g-4)
    c: Tangent(g3,g0)
    c: Tangent(g1,g-3)
    c: Coincident(g5,g1)
    c: PointOnObject(g5,g-7)
    c: Coincident(g6,g5)
    c: PointOnObject(g6,g-8)
    c: Vertical(g6)
    c: Coincident(g7,g6)
    c: Coincident(g7,g1)
    c: Tangent(g6,g1)
FEATURE [PartDesign::AdditiveLoft] AdditiveLoft014
  BaseFeature = -> AdditiveLoft013
  Closed = false
  Profile = -> Sketch311
  Refine = true
  Ruled = false
  Sections = -> [Sketch312]
  Suppressed = false
FEATURE [Sketcher::SketchObject] Sketch313
  ArcFitTolerance = 1e-06
  AttachmentSupport = -> [AdditiveLoft014]
  ExternalGeometry = -> [AdditiveLoft014]
  FullyConstrained = true
  MakeInternals = false
  MapMode = 5
  Placement = pos=(0,0,0) rot=(1,0,0;3.14159rad)
  sketch-geometry (8):
    g0: LineSegment StartX=66.5 StartY=-2.70416 StartZ=0 EndX=66.5 EndY=-3.70416 EndZ=0
    g1: LineSegment StartX=66.5 StartY=-3.70416 StartZ=0 EndX=65.5 EndY=-3.70416 EndZ=0
    g2: LineSegment StartX=65.5 StartY=-2.70416 StartZ=0 EndX=65.5 EndY=-3.70416 EndZ=0
    g3: ArcOfCircle CenterX=66 CenterY=7.21338e-09 CenterZ=0 NormalX=0 NormalY=0 NormalZ=1 AngleXU=0 Radius=2.75 StartAngle=4.52955 EndAngle=4.89522
    g4: ArcOfCircle CenterX=74.1 CenterY=0 CenterZ=0 NormalX=0 NormalY=0 NormalZ=1 AngleXU=0 Radius=2.75 StartAngle=4.52955 EndAngle=4.89522
    g5: LineSegment StartX=74.6 StartY=-2.70416 StartZ=0 EndX=74.6 EndY=-3.70416 EndZ=0
    g6: LineSegment StartX=74.6 StartY=-3.70416 StartZ=0 EndX=73.6 EndY=-3.70416 EndZ=0
    g7: LineSegment StartX=73.6 StartY=-2.70416 StartZ=0 EndX=73.6 EndY=-3.70416 EndZ=0
  constraints (25):
    c: PointOnObject(g0,g-4)
    c: Vertical(g0)
    c: Coincident(g1,g0)
    c: Horizontal(g1)
    c: Coincident(g2,g1)
    c: Vertical(g2)
    c: DistanceX(g1,g1) = 1
    c: DistanceY(g2,g2) = 1
    c: Coincident(g3,g0)
    c: Coincident(g3,g2)
    c: Tangent(g3,g-4)
    c: PointOnObject(g2,g-4)
    c: DistanceX(g2,g3) = 0.5
    c: PointOnObject(g4,g-3)
    c: Coincident(g4,g-3)
    c: Coincident(g6,g5)
    c: Horizontal(g6)
    c: Coincident(g7,g4)
    c: Coincident(g7,g6)
    c: Vertical(g5)
    c: Vertical(g7)
    c: DistanceX(g6,g6) = 1
    c: Coincident(g5,g4)
    c: DistanceY(g7,g7) = 1
    c: DistanceX(g4,g4) = 0.5
FEATURE [Sketcher::SketchObject] Sketch314
  ArcFitTolerance = 1e-06
  AttachmentSupport = -> [AdditiveLoft014]
  ExternalGeometry = -> [AdditiveLoft014,Sketch313]
  FullyConstrained = true
  MakeInternals = false
  MapMode = 5
  Placement = pos=(0,0,-4.2) rot=(1,0,0;3.14159rad)
  sketch-geometry (8):
    g0: ArcOfCircle CenterX=66 CenterY=-4.19825e-06 CenterZ=0 NormalX=0 NormalY=0 NormalZ=1 AngleXU=0 Radius=2.75 StartAngle=4.52955 EndAngle=4.89522
    g1: ArcOfCircle CenterX=74.1 CenterY=-1.07947e-05 CenterZ=0 NormalX=0 NormalY=0 NormalZ=1 AngleXU=0 Radius=2.74999 StartAngle=4.52955 EndAngle=4.89522
    g2: LineSegment StartX=66.5 StartY=-2.70416 StartZ=0 EndX=66.5 EndY=-2.75 EndZ=0
    g3: LineSegment StartX=65.5 StartY=-2.70416 StartZ=0 EndX=65.5 EndY=-2.75 EndZ=0
    g4: LineSegment StartX=65.5 StartY=-2.75 StartZ=0 EndX=66.5 EndY=-2.75 EndZ=0
    g5: LineSegment StartX=73.6 StartY=-2.70416 StartZ=0 EndX=73.6 EndY=-2.75 EndZ=0
    g6: LineSegment StartX=74.6 StartY=-2.70416 StartZ=0 EndX=74.6 EndY=-2.75 EndZ=0
    g7: LineSegment StartX=74.6 StartY=-2.75 StartZ=0 EndX=73.6 EndY=-2.75 EndZ=0
  constraints (22):
    c: Coincident(g0,g-5)
    c: Coincident(g0,g-6)
    c: Coincident(g1,g-7)
    c: Coincident(g1,g-8)
    c: Tangent(g1,g-3)
    c: Tangent(g0,g-4)
    c: Coincident(g2,g0)
    c: PointOnObject(g2,g-6)
    c: Coincident(g3,g0)
    c: PointOnObject(g3,g-5)
    c: Coincident(g4,g3)
    c: Coincident(g4,g2)
    c: Horizontal(g4)
    c: Tangent(g4,g0)
    c: Coincident(g5,g1)
    c: PointOnObject(g5,g-7)
    c: Coincident(g6,g1)
    c: PointOnObject(g6,g-8)
    c: Coincident(g7,g6)
    c: Coincident(g7,g5)
    c: Horizontal(g7)
    c: Tangent(g7,g1)
FEATURE [PartDesign::AdditiveLoft] AdditiveLoft015
  BaseFeature = -> AdditiveLoft014
  Closed = false
  Profile = -> Sketch313
  Refine = true
  Ruled = false
  Sections = -> [Sketch314]
  Suppressed = false
FEATURE [Sketcher::SketchObject] Sketch315
  ArcFitTolerance = 1e-06
  AttachmentSupport = -> [AdditiveLoft015]
  ExternalGeometry = -> [AdditiveLoft015]
  FullyConstrained = true
  MakeInternals = false
  MapMode = 5
  Placement = pos=(0,0,0) rot=(1,0,0;3.14159rad)
  sketch-geometry (4):
    g0: LineSegment StartX=68.75 StartY=0.375 StartZ=0 EndX=68.75 EndY=-0.375 EndZ=0
    g1: LineSegment StartX=68.75 StartY=-0.375 StartZ=0 EndX=71.2 EndY=-0.375 EndZ=0
    g2: LineSegment StartX=71.2 StartY=-0.375 StartZ=0 EndX=71.2 EndY=0.375 EndZ=0
    g3: LineSegment StartX=71.2 StartY=0.375 StartZ=0 EndX=68.75 EndY=0.375 EndZ=0
  constraints (13):
    c: Coincident(g0,g1)
    c: Coincident(g1,g2)
    c: Coincident(g2,g3)
    c: Coincident(g3,g0)
    c: Vertical(g0)
    c: Vertical(g2)
    c: Horizontal(g1)
    c: Horizontal(g3)
    c: DistanceX(g-3,g0) = 0
    c: DistanceX(g2,g-4) = 0.15
    c: DistanceY(g2,g2) = 0.75
    c: DistanceY(g-5,g-5) = 1
    c: DistanceY(g2,g-4) = 0.125
FEATURE [PartDesign::Pad] Pad209
  BaseFeature = -> AdditiveLoft015
  Direction = (0,0,-1)
  Length = 2.7
  Length2 = 10
  Profile = -> Sketch315
  ReferenceAxis = -> Sketch315 [N_Axis]
  Refine = true
  Suppressed = false
  Type = 0
FEATURE [Sketcher::SketchObject] Sketch316
  ArcFitTolerance = 1e-06
  AttachmentSupport = -> [Pad209]
  ExternalGeometry = -> [Pad209]
  FullyConstrained = true
  MakeInternals = false
  MapMode = 5
  Placement = pos=(0,0,-4.2) rot=(1,0,0;3.14159rad)
  sketch-geometry (2):
    g0: Circle CenterX=66 CenterY=0 CenterZ=0 NormalX=0 NormalY=0 NormalZ=1 AngleXU=0 Radius=2.15
    g1: Circle CenterX=74.1 CenterY=0 CenterZ=0 NormalX=0 NormalY=0 NormalZ=1 AngleXU=0 Radius=2.15
  constraints (4):
    c: Coincident(g0,g-4)
    c: Coincident(g1,g-3)
    c: Radius(g0) = 2.15
    c: Radius(g1) = 2.15
FEATURE [PartDesign::Pad] Pad210
  BaseFeature = -> Pad209
  Direction = (0,0,-1)
  Length = 4.5
  Length2 = 10
  Profile = -> Sketch316
  ReferenceAxis = -> Sketch316 [N_Axis]
  Refine = true
  Suppressed = false
  Type = 0
FEATURE [PartDesign::Fillet] Fillet038
  Base = -> Pad210 [Edge138,Edge140]
  BaseFeature = -> Pad210
  Radius = 0.5
  Refine = true
  SupportTransform = false
  Suppressed = false
  UseAllEdges = false
FEATURE [Sketcher::SketchObject] Sketch317
  ArcFitTolerance = 1e-06
  AttachmentSupport = -> [Fillet038]
  ExternalGeometry = -> [Fillet038]
  FullyConstrained = true
  MakeInternals = false
  MapMode = 5
  Placement = pos=(0,0,-8.7) rot=(1,0,0;3.14159rad)
  sketch-geometry (2):
    g0: Circle CenterX=66 CenterY=0 CenterZ=0 NormalX=0 NormalY=0 NormalZ=1 AngleXU=0 Radius=1.38
    g1: Circle CenterX=74.1 CenterY=0 CenterZ=0 NormalX=0 NormalY=0 NormalZ=1 AngleXU=0 Radius=1.38
  constraints (4):
    c: Coincident(g0,g-4)
    c: Coincident(g1,g-3)
    c: Radius(g0) = 1.38
    c: Radius(g1) = 1.38
FEATURE [PartDesign::Pad] Pad211
  BaseFeature = -> Fillet038
  Direction = (0,0,-1)
  Length = 4.5
  Length2 = 10
  Profile = -> Sketch317
  ReferenceAxis = -> Sketch317 [N_Axis]
  Refine = true
  Suppressed = false
  Type = 0
FEATURE [PartDesign::Fillet] Fillet039
  Base = -> Pad211 [Edge60,Edge150]
  BaseFeature = -> Pad211
  Radius = 0.5
  Refine = true
  SupportTransform = false
  Suppressed = false
  UseAllEdges = false
FEATURE [PartDesign::Body] Body022  label="Mixmaster_Dual_Head_Missile"
  AllowCompound = false
  Group = -> [Sketch302,Pad204,Sketch303,Pad205,Sketch304,Pad206,Sketch305,Pad207,Fillet036,Fillet037,Sketch306,Pad208,Sketch307,Sketch308,AdditiveLoft012,Sketch309,Sketch310,AdditiveLoft013,Sketch311,Sketch312,AdditiveLoft014,Sketch313,Sketch314,AdditiveLoft015,Sketch315,Pad209,Sketch316,Pad210,Fillet038,Sketch317,Pad211,Fillet039]
  Origin = -> Origin024
  Placement = pos=(101.05,-5,-14.9) rot=(0,1,0;3.14159rad)
  Tip = -> Fillet039
COMPONENT P6 — recipe-attached ("Mixmaster_Single_Head_Missile", modeled in this document).
Construction recipe (the document's own serialized feature program — sketch geometry with constraints, then the solid features built on it; lengths are millimeters unless a unit is written):

FEATURE [Sketcher::SketchObject] Sketch318
  ArcFitTolerance = 1e-06
  AttachmentOffset = pos=(62,0,-10) rot=(0,0,1;0rad)
  AttachmentSupport = -> [XY_Plane025]
  FullyConstrained = true
  MakeInternals = false
  MapMode = 5
  Placement = pos=(62,0,-10) rot=(0,0,1;0rad)
  sketch-geometry (1):
    g0: Circle CenterX=0 CenterY=0 CenterZ=0 NormalX=0 NormalY=0 NormalZ=1 AngleXU=0 Radius=4.05
  constraints (2):
    c: Coincident(g0,g-1)
    c: Radius(g0) = 4.05
FEATURE [PartDesign::Pad] Pad212
  Direction = (0,0,1)
  Length = 1.9
  Length2 = 10
  Profile = -> Sketch318
  ReferenceAxis = -> Sketch318 [N_Axis]
  Refine = true
  Suppressed = false
  Type = 0
FEATURE [Sketcher::SketchObject] Sketch319
  ArcFitTolerance = 1e-06
  AttachmentSupport = -> [Pad212]
  ExternalGeometry = -> [Pad212]
  FullyConstrained = true
  MakeInternals = false
  MapMode = 5
  Placement = pos=(0,0,-8.1) rot=(0,0,1;0rad)
  sketch-geometry (1):
    g0: Circle CenterX=62 CenterY=0 CenterZ=0 NormalX=0 NormalY=0 NormalZ=1 AngleXU=0 Radius=2.05
  constraints (2):
    c: Coincident(g0,g-3)
    c: Radius(g0) = 2.05
FEATURE [PartDesign::Pad] Pad213
  BaseFeature = -> Pad212
  Direction = (0,0,1)
  Length = 16.4
  Length2 = 10
  Profile = -> Sketch319
  ReferenceAxis = -> Sketch319 [N_Axis]
  Refine = true
  Suppressed = false
  Type = 0
FEATURE [Sketcher::SketchObject] Sketch320
  ArcFitTolerance = 1e-06
  AttachmentSupport = -> [Pad213]
  ExternalGeometry = -> [Pad213]
  FullyConstrained = true
  MakeInternals = false
  MapMode = 5
  Placement = pos=(0,0,8.3) rot=(0,0,1;0rad)
  sketch-geometry (1):
    g0: Circle CenterX=62 CenterY=0 CenterZ=0 NormalX=0 NormalY=0 NormalZ=1 AngleXU=0 Radius=1.15
  constraints (2):
    c: Coincident(g0,g-3)
    c: Radius(g0) = 1.15
FEATURE [PartDesign::Pad] Pad214
  BaseFeature = -> Pad213
  Direction = (0,0,1)
  Length = 2.5
  Length2 = 10
  Profile = -> Sketch320
  ReferenceAxis = -> Sketch320 [N_Axis]
  Refine = true
  Suppressed = false
  Type = 0
FEATURE [Sketcher::SketchObject] Sketch321
  ArcFitTolerance = 1e-06
  AttachmentSupport = -> [Pad214]
  ExternalGeometry = -> [Pad214]
  FullyConstrained = true
  MakeInternals = false
  MapMode = 5
  Placement = pos=(0,0,10.8) rot=(0,0,1;0rad)
  sketch-geometry (1):
    g0: Circle CenterX=62 CenterY=0 CenterZ=0 NormalX=0 NormalY=0 NormalZ=1 AngleXU=0 Radius=2.05
  constraints (2):
    c: Coincident(g0,g-3)
    c: Equal(g0,g-3)
FEATURE [PartDesign::Pad] Pad215
  BaseFeature = -> Pad214
  Direction = (0,0,1)
  Length = 2.6
  Length2 = 10
  Profile = -> Sketch321
  ReferenceAxis = -> Sketch321 [N_Axis]
  Refine = true
  Suppressed = false
  Type = 0
FEATURE [PartDesign::Fillet] Fillet040
  Base = -> Pad215 [Edge12]
  BaseFeature = -> Pad215
  Radius = 0.5
  Refine = true
  SupportTransform = false
  Suppressed = false
  UseAllEdges = false
FEATURE [PartDesign::Fillet] Fillet041
  Base = -> Fillet040 [Edge14]
  BaseFeature = -> Fillet040
  Radius = 0.2
  Refine = true
  SupportTransform = false
  Suppressed = false
  UseAllEdges = false
FEATURE [Sketcher::SketchObject] Sketch322
  ArcFitTolerance = 1e-06
  AttachmentSupport = -> [Fillet041]
  ExternalGeometry = -> [Fillet041]
  FullyConstrained = true
  MakeInternals = false
  MapMode = 5
  Placement = pos=(0,0,-10) rot=(1,0,0;3.14159rad)
  sketch-geometry (1):
    g0: Circle CenterX=62 CenterY=0 CenterZ=0 NormalX=0 NormalY=0 NormalZ=1 AngleXU=0 Radius=2.75
  constraints (2):
    c: Coincident(g0,g-3)
    c: Radius(g0) = 2.75
FEATURE [PartDesign::Pad] Pad216
  BaseFeature = -> Fillet041
  Direction = (0,0,-1)
  Length = 4.2
  Length2 = 10
  Profile = -> Sketch322
  ReferenceAxis = -> Sketch322 [N_Axis]
  Refine = true
  Suppressed = false
  Type = 0
FEATURE [Sketcher::SketchObject] Sketch323
  ArcFitTolerance = 1e-06
  AttachmentSupport = -> [Pad216]
  ExternalGeometry = -> [Pad216]
  FullyConstrained = true
  MakeInternals = false
  MapMode = 5
  Placement = pos=(0,0,-10) rot=(1,0,0;3.14159rad)
  sketch-geometry (4):
    g0: ArcOfCircle CenterX=62 CenterY=-2.4362e-12 CenterZ=0 NormalX=0 NormalY=0 NormalZ=1 AngleXU=0 Radius=2.75 StartAngle=2.95876 EndAngle=3.32443
    g1: LineSegment StartX=59.2958 StartY=0.5 StartZ=0 EndX=58.2958 EndY=0.5 EndZ=0
    g2: LineSegment StartX=58.2958 StartY=0.5 StartZ=0 EndX=58.2958 EndY=-0.5 EndZ=0
    g3: LineSegment StartX=58.2958 StartY=-0.5 StartZ=0 EndX=59.2958 EndY=-0.5 EndZ=0
  constraints (12):
    c: Tangent(g0,g-3) = -1.5708
    c: PointOnObject(g0,g-3)
    c: Coincident(g1,g0)
    c: Horizontal(g1)
    c: Coincident(g2,g1)
    c: Vertical(g2)
    c: Coincident(g3,g2)
    c: Coincident(g3,g0)
    c: Horizontal(g3)
    c: DistanceX(g1,g1) = 1
    c: DistanceY(g2,g2) = 1
    c: DistanceY(g0,g0) = 0.5
FEATURE [Sketcher::SketchObject] Sketch324
  ArcFitTolerance = 1e-06
  AttachmentSupport = -> [Pad216]
  ExternalGeometry = -> [Pad216,Sketch323]
  FullyConstrained = true
  MakeInternals = false
  MapMode = 5
  Placement = pos=(0,0,-14.2) rot=(1,0,0;3.14159rad)
  sketch-geometry (4):
    g0: ArcOfCircle CenterX=62 CenterY=-1e-16 CenterZ=0 NormalX=0 NormalY=0 NormalZ=1 AngleXU=0 Radius=2.75 StartAngle=2.95876 EndAngle=3.32443
    g1: LineSegment StartX=59.2958 StartY=0.5 StartZ=0 EndX=59.25 EndY=0.5 EndZ=0
    g2: LineSegment StartX=59.25 StartY=0.5 StartZ=0 EndX=59.25 EndY=-0.5 EndZ=0
    g3: LineSegment StartX=59.25 StartY=-0.5 StartZ=0 EndX=59.2958 EndY=-0.5 EndZ=0
  constraints (11):
    c: Coincident(g0,g-6)
    c: Coincident(g0,g-7)
    c: Coincident(g0,g-3)
    c: Coincident(g1,g0)
    c: PointOnObject(g1,g-6)
    c: Coincident(g2,g1)
    c: PointOnObject(g2,g-7)
    c: Vertical(g2)
    c: Coincident(g3,g2)
    c: Coincident(g3,g0)
    c: Tangent(g2,g0)
FEATURE [PartDesign::AdditiveLoft] AdditiveLoft016
  BaseFeature = -> Pad216
  Closed = false
  Profile = -> Sketch324
  Refine = true
  Ruled = false
  Sections = -> [Sketch323]
  Suppressed = false
FEATURE [Sketcher::SketchObject] Sketch325
  ArcFitTolerance = 1e-06
  AttachmentSupport = -> [AdditiveLoft016]
  ExternalGeometry = -> [AdditiveLoft016]
  FullyConstrained = true
  MakeInternals = false
  MapMode = 5
  Placement = pos=(0,0,-10) rot=(1,0,0;3.14159rad)
  sketch-geometry (4):
    g0: ArcOfCircle CenterX=62 CenterY=-4.1e-15 CenterZ=0 NormalX=0 NormalY=0 NormalZ=1 AngleXU=0 Radius=2.75 StartAngle=6.10035 EndAngle=6.46602
    g1: LineSegment StartX=64.7042 StartY=0.5 StartZ=0 EndX=65.7042 EndY=0.5 EndZ=0
    g2: LineSegment StartX=65.7042 StartY=0.5 StartZ=0 EndX=65.7042 EndY=-0.5 EndZ=0
    g3: LineSegment StartX=65.7042 StartY=-0.5 StartZ=0 EndX=64.7042 EndY=-0.5 EndZ=0
  constraints (12):
    c: PointOnObject(g0,g-3)
    c: Tangent(g0,g-4) = -1.5708
    c: Coincident(g1,g0)
    c: Coincident(g2,g1)
    c: Vertical(g2)
    c: Coincident(g3,g2)
    c: Coincident(g3,g0)
    c: Horizontal(g3)
    c: Horizontal(g1)
    c: DistanceY(g2,g2) = 1
    c: DistanceX(g1,g1) = 1
    c: DistanceY(g0,g0) = 0.5
FEATURE [Sketcher::SketchObject] Sketch326
  ArcFitTolerance = 1e-06
  AttachmentSupport = -> [AdditiveLoft016]
  ExternalGeometry = -> [AdditiveLoft016,Sketch325]
  FullyConstrained = true
  MakeInternals = false
  MapMode = 5
  Placement = pos=(0,0,-14.2) rot=(1,0,0;3.14159rad)
  sketch-geometry (4):
    g0: ArcOfCircle CenterX=62 CenterY=0 CenterZ=0 NormalX=0 NormalY=0 NormalZ=1 AngleXU=0 Radius=2.75 StartAngle=6.10035 EndAngle=6.46602
    g1: LineSegment StartX=64.7042 StartY=0.5 StartZ=0 EndX=64.75 EndY=0.5 EndZ=0
    g2: LineSegment StartX=64.7042 StartY=-0.5 StartZ=0 EndX=64.75 EndY=-0.5 EndZ=0
    g3: LineSegment StartX=64.75 StartY=-0.5 StartZ=0 EndX=64.75 EndY=0.5 EndZ=0
  constraints (11):
    c: Coincident(g0,g-6)
    c: Coincident(g0,g-4)
    c: PointOnObject(g0,g-5)
    c: Coincident(g1,g0)
    c: PointOnObject(g1,g-5)
    c: Coincident(g2,g0)
    c: PointOnObject(g2,g-6)
    c: Coincident(g3,g2)
    c: Coincident(g3,g1)
    c: Vertical(g3)
    c: Tangent(g3,g0)
FEATURE [PartDesign::AdditiveLoft] AdditiveLoft017
  BaseFeature = -> AdditiveLoft016
  Closed = false
  Profile = -> Sketch326
  Refine = true
  Ruled = false
  Sections = -> [Sketch325]
  Suppressed = false
FEATURE [Sketcher::SketchObject] Sketch327
  ArcFitTolerance = 1e-06
  AttachmentSupport = -> [AdditiveLoft017]
  ExternalGeometry = -> [AdditiveLoft017]
  FullyConstrained = true
  MakeInternals = false
  MapMode = 5
  Placement = pos=(0,0,-10) rot=(1,0,0;3.14159rad)
  sketch-geometry (4):
    g0: ArcOfCircle CenterX=62 CenterY=0 CenterZ=0 NormalX=0 NormalY=0 NormalZ=1 AngleXU=0 Radius=2.74999 StartAngle=4.52955 EndAngle=4.89522
    g1: LineSegment StartX=62.5 StartY=-2.70415 StartZ=0 EndX=62.5 EndY=-3.70415 EndZ=0
    g2: LineSegment StartX=62.5 StartY=-3.70415 StartZ=0 EndX=61.5 EndY=-3.70415 EndZ=0
    g3: LineSegment StartX=61.5 StartY=-2.70415 StartZ=0 EndX=61.5 EndY=-3.70415 EndZ=0
  constraints (12):
    c: Coincident(g0,g-3)
    c: Coincident(g1,g0)
    c: Vertical(g1)
    c: Coincident(g2,g1)
    c: Coincident(g3,g2)
    c: Vertical(g3)
    c: Horizontal(g2)
    c: DistanceX(g2,g2) = 1
    c: DistanceY(g1,g1) = 1
    c: DistanceX(g0,g0) = 0.5
    c: Coincident(g0,g3)
    c: Tangent(g0,g-3)
FEATURE [Sketcher::SketchObject] Sketch328
  ArcFitTolerance = 1e-06
  AttachmentSupport = -> [AdditiveLoft017]
  ExternalGeometry = -> [AdditiveLoft017,Sketch327]
  FullyConstrained = true
  MakeInternals = false
  MapMode = 5
  Placement = pos=(0,0,-14.2) rot=(1,0,0;3.14159rad)
  sketch-geometry (4):
    g0: ArcOfCircle CenterX=62 CenterY=-0.000540384 CenterZ=0 NormalX=0 NormalY=0 NormalZ=1 AngleXU=0 Radius=2.74946 StartAngle=4.52952 EndAngle=4.89526
    g1: LineSegment StartX=61.5 StartY=-2.70415 StartZ=0 EndX=61.5 EndY=-2.75 EndZ=0
    g2: LineSegment StartX=62.5 StartY=-2.70415 StartZ=0 EndX=62.5 EndY=-2.75 EndZ=0
    g3: LineSegment StartX=62.5 StartY=-2.75 StartZ=0 EndX=61.5 EndY=-2.75 EndZ=0
  constraints (11):
    c: Coincident(g0,g-4)
    c: Coincident(g0,g-5)
    c: Tangent(g0,g-3)
    c: Coincident(g1,g0)
    c: PointOnObject(g1,g-4)
    c: Coincident(g2,g0)
    c: PointOnObject(g2,g-5)
    c: Coincident(g3,g2)
    c: Coincident(g3,g1)
    c: Horizontal(g3)
    c: Tangent(g3,g0)
FEATURE [PartDesign::AdditiveLoft] AdditiveLoft018
  BaseFeature = -> AdditiveLoft017
  Closed = false
  Profile = -> Sketch328
  Refine = true
  Ruled = false
  Sections = -> [Sketch327]
  Suppressed = false
FEATURE [Sketcher::SketchObject] Sketch329
  ArcFitTolerance = 1e-06
  AttachmentSupport = -> [AdditiveLoft018]
  ExternalGeometry = -> [AdditiveLoft018]
  FullyConstrained = true
  MakeInternals = false
  MapMode = 5
  Placement = pos=(0,0,-10) rot=(1,0,0;3.14159rad)
  sketch-geometry (4):
    g0: ArcOfCircle CenterX=62 CenterY=0 CenterZ=0 NormalX=0 NormalY=0 NormalZ=1 AngleXU=0 Radius=2.75 StartAngle=1.38796 EndAngle=1.75363
    g1: LineSegment StartX=61.5 StartY=2.70416 StartZ=0 EndX=61.5 EndY=3.70416 EndZ=0
    g2: LineSegment StartX=61.5 StartY=3.70416 StartZ=0 EndX=62.5 EndY=3.70416 EndZ=0
    g3: LineSegment StartX=62.5 StartY=2.70416 StartZ=0 EndX=62.5 EndY=3.70416 EndZ=0
  constraints (12):
    c: PointOnObject(g0,g-3)
    c: Coincident(g0,g-3)
    c: Coincident(g1,g0)
    c: Vertical(g1)
    c: Coincident(g2,g1)
    c: Horizontal(g2)
    c: Coincident(g3,g0)
    c: Coincident(g3,g2)
    c: Vertical(g3)
    c: DistanceX(g2,g2) = 1
    c: DistanceY(g3,g3) = 1
    c: DistanceX(g0,g0) = 0.5
FEATURE [Sketcher::SketchObject] Sketch330
  ArcFitTolerance = 1e-06
  AttachmentSupport = -> [AdditiveLoft018]
  ExternalGeometry = -> [AdditiveLoft018,Sketch329]
  FullyConstrained = true
  MakeInternals = false
  MapMode = 5
  Placement = pos=(0,0,-14.2) rot=(1,0,0;3.14159rad)
  sketch-geometry (4):
    g0: ArcOfCircle CenterX=62 CenterY=0 CenterZ=0 NormalX=0 NormalY=0 NormalZ=1 AngleXU=0 Radius=2.75 StartAngle=1.38796 EndAngle=1.75363
    g1: LineSegment StartX=61.5 StartY=2.70416 StartZ=0 EndX=61.5 EndY=2.75 EndZ=0
    g2: LineSegment StartX=62.5 StartY=2.70416 StartZ=0 EndX=62.5 EndY=2.75 EndZ=0
    g3: LineSegment StartX=62.5 StartY=2.75 StartZ=0 EndX=61.5 EndY=2.75 EndZ=0
  constraints (11):
    c: Coincident(g0,g-5)
    c: Coincident(g0,g-4)
    c: Coincident(g0,g-3)
    c: Coincident(g1,g0)
    c: PointOnObject(g1,g-5)
    c: Coincident(g2,g0)
    c: PointOnObject(g2,g-4)
    c: Coincident(g3,g2)
    c: Coincident(g3,g1)
    c: Horizontal(g3)
    c: Tangent(g3,g0)
FEATURE [PartDesign::AdditiveLoft] AdditiveLoft019
  BaseFeature = -> AdditiveLoft018
  Closed = false
  Profile = -> Sketch329
  Refine = true
  Ruled = false
  Sections = -> [Sketch330]
  Suppressed = false
FEATURE [Sketcher::SketchObject] Sketch331
  ArcFitTolerance = 1e-06
  AttachmentSupport = -> [AdditiveLoft019]
  ExternalGeometry = -> [AdditiveLoft019]
  FullyConstrained = true
  MakeInternals = false
  MapMode = 5
  Placement = pos=(0,0,-14.2) rot=(1,0,0;3.14159rad)
  sketch-geometry (1):
    g0: Circle CenterX=62 CenterY=0 CenterZ=0 NormalX=0 NormalY=0 NormalZ=1 AngleXU=0 Radius=2.15
  constraints (2):
    c: Coincident(g0,g-3)
    c: Radius(g0) = 2.15
FEATURE [PartDesign::Pad] Pad217
  BaseFeature = -> AdditiveLoft019
  Direction = (0,0,-1)
  Length = 4.5
  Length2 = 10
  Profile = -> Sketch331
  ReferenceAxis = -> Sketch331 [N_Axis]
  Refine = true
  Suppressed = false
  Type = 0
FEATURE [PartDesign::Fillet] Fillet042
  Base = -> Pad217 [Edge62]
  BaseFeature = -> Pad217
  Radius = 0.5
  Refine = true
  SupportTransform = false
  Suppressed = false
  UseAllEdges = false
FEATURE [Sketcher::SketchObject] Sketch332
  ArcFitTolerance = 1e-06
  AttachmentSupport = -> [Fillet042]
  ExternalGeometry = -> [Fillet042]
  FullyConstrained = true
  MakeInternals = false
  MapMode = 5
  Placement = pos=(0,0,-18.7) rot=(1,0,0;3.14159rad)
  sketch-geometry (1):
    g0: Circle CenterX=62 CenterY=0 CenterZ=0 NormalX=0 NormalY=0 NormalZ=1 AngleXU=0 Radius=1.38
  constraints (2):
    c: Coincident(g0,g-3)
    c: Radius(g0) = 1.38
FEATURE [PartDesign::Pad] Pad218
  BaseFeature = -> Fillet042
  Direction = (0,0,-1)
  Length = 4.5
  Length2 = 10
  Profile = -> Sketch332
  ReferenceAxis = -> Sketch332 [N_Axis]
  Refine = true
  Suppressed = false
  Type = 0
FEATURE [PartDesign::Fillet] Fillet043
  Base = -> Pad218 [Edge56]
  BaseFeature = -> Pad218
  Radius = 0.5
  Refine = true
  SupportTransform = false
  Suppressed = false
  UseAllEdges = false
FEATURE [PartDesign::Body] Body023  label="Mixmaster_Single_Head_Missile"
  AllowCompound = false
  Group = -> [Sketch318,Pad212,Sketch319,Pad213,Sketch320,Pad214,Sketch321,Pad215,Fillet040,Fillet041,Sketch322,Pad216,Sketch323,Sketch324,AdditiveLoft016,Sketch325,Sketch326,AdditiveLoft017,Sketch327,Sketch328,AdditiveLoft018,Sketch329,Sketch330,AdditiveLoft019,Sketch331,Pad217,Fillet042,Sketch332,Pad218,Fillet043]
  Origin = -> Origin025
  Placement = pos=(113,-5,-25.1) rot=(0,1,0;3.14159rad)
  Tip = -> Fillet043
COMPONENT P7 — recipe-attached ("Hook_Gun", modeled in this document).
Construction recipe (the document's own serialized feature program — sketch geometry with constraints, then the solid features built on it; lengths are millimeters unless a unit is written):

FEATURE [Sketcher::SketchObject] Sketch333
  ArcFitTolerance = 1e-06
  AttachmentSupport = -> [XY_Plane026]
  FullyConstrained = true
  MakeInternals = false
  MapMode = 5
  sketch-geometry (4):
    g0: LineSegment StartX=0 StartY=0 StartZ=0 EndX=10.2 EndY=0 EndZ=0
    g1: LineSegment StartX=10.2 StartY=0 StartZ=0 EndX=10.2 EndY=6 EndZ=0
    g2: LineSegment StartX=10.2 StartY=6 StartZ=0 EndX=0 EndY=6 EndZ=0
    g3: LineSegment StartX=0 StartY=6 StartZ=0 EndX=0 EndY=0 EndZ=0
  constraints (11):
    c: Coincident(g0,g1)
    c: Coincident(g1,g2)
    c: Coincident(g2,g3)
    c: Coincident(g3,g0)
    c: Horizontal(g0)
    c: Horizontal(g2)
    c: Vertical(g1)
    c: Vertical(g3)
    c: Coincident(g0,g-1)
    c: DistanceX(g2,g2) = 10.2
    c: DistanceY(g1,g1) = 6
FEATURE [PartDesign::Pad] Pad219
  Direction = (0,0,1)
  Length = 4
  Length2 = 10
  Profile = -> Sketch333
  ReferenceAxis = -> Sketch333 [N_Axis]
  Refine = true
  Suppressed = false
  Type = 0
FEATURE [Sketcher::SketchObject] Sketch334
  ArcFitTolerance = 1e-06
  AttachmentSupport = -> [Pad219]
  ExternalGeometry = -> [Pad219]
  FullyConstrained = false
  MakeInternals = false
  MapMode = 5
  Placement = pos=(0,0,0) rot=(1,0,0;1.5708rad)
  sketch-geometry (20):
    g0: LineSegment StartX=2.2 StartY=4 StartZ=0 EndX=2.2 EndY=0 EndZ=0
    g1: LineSegment StartX=2.2 StartY=0 StartZ=0 EndX=2.7 EndY=0 EndZ=0
    g2: LineSegment StartX=2.7 StartY=0 StartZ=0 EndX=2.7 EndY=4 EndZ=0
    g3: LineSegment StartX=2.7 StartY=4 StartZ=0 EndX=2.2 EndY=4 EndZ=0
    g4: LineSegment StartX=3.7 StartY=4 StartZ=0 EndX=3.7 EndY=0 EndZ=0
    g5: LineSegment StartX=3.7 StartY=0 StartZ=0 EndX=4.2 EndY=0 EndZ=0
    g6: LineSegment StartX=4.2 StartY=0 StartZ=0 EndX=4.2 EndY=4 EndZ=0
    g7: LineSegment StartX=4.2 StartY=4 StartZ=0 EndX=3.7 EndY=4 EndZ=0
    g8: LineSegment StartX=5.2 StartY=4 StartZ=0 EndX=5.2 EndY=0 EndZ=0
    g9: LineSegment StartX=5.2 StartY=0 StartZ=0 EndX=5.7 EndY=0 EndZ=0
    g10: LineSegment StartX=5.7 StartY=0 StartZ=0 EndX=5.7 EndY=4 EndZ=0
    g11: LineSegment StartX=5.7 StartY=4 StartZ=0 EndX=5.2 EndY=4 EndZ=0
    g12: LineSegment StartX=6.7 StartY=4 StartZ=0 EndX=6.7 EndY=0 EndZ=0
    g13: LineSegment StartX=6.7 StartY=0 StartZ=0 EndX=7.2 EndY=0 EndZ=0
    g14: LineSegment StartX=7.2 StartY=0 StartZ=0 EndX=7.2 EndY=4 EndZ=0
    g15: LineSegment StartX=7.2 StartY=4 StartZ=0 EndX=6.7 EndY=4 EndZ=0
    g16: LineSegment StartX=8.2 StartY=4 StartZ=0 EndX=8.2 EndY=0 EndZ=0
    g17: LineSegment StartX=8.2 StartY=0 StartZ=0 EndX=8.7 EndY=0 EndZ=0
    g18: LineSegment StartX=8.7 StartY=0 StartZ=0 EndX=8.7 EndY=4 EndZ=0
    g19: LineSegment StartX=8.7 StartY=4 StartZ=0 EndX=8.2 EndY=4 EndZ=0
  constraints (60):
    c: Coincident(g0,g1)
    c: Coincident(g1,g2)
    c: Coincident(g2,g3)
    c: Coincident(g3,g0)
    c: Vertical(g0)
    c: Vertical(g2)
    c: Horizontal(g1)
    c: Horizontal(g3)
    c: PointOnObject(g0,g-3)
    c: PointOnObject(g1,g-5)
    c: Coincident(g4,g5)
    c: Coincident(g5,g6)
    c: Coincident(g6,g7)
    c: Coincident(g7,g4)
    c: Vertical(g4)
    c: Vertical(g6)
    c: Horizontal(g5)
    c: Horizontal(g7)
    c: PointOnObject(g4,g-3)
    c: PointOnObject(g5,g-5)
    c: Coincident(g8,g9)
    c: Coincident(g9,g10)
    c: Coincident(g10,g11)
    c: Coincident(g11,g8)
    c: Vertical(g8)
    c: Vertical(g10)
    c: Horizontal(g9)
    c: Horizontal(g11)
    c: PointOnObject(g9,g-5)
    c: Coincident(g12,g13)
    c: Coincident(g13,g14)
    c: Coincident(g14,g15)
    c: Coincident(g15,g12)
    c: Vertical(g12)
    c: Vertical(g14)
    c: Horizontal(g13)
    c: Horizontal(g15)
    c: PointOnObject(g12,g-3)
    c: Coincident(g16,g17)
    c: Coincident(g17,g18)
    c: Coincident(g18,g19)
    c: Coincident(g19,g16)
    c: Vertical(g16)
    c: Vertical(g18)
    c: Horizontal(g17)
    c: Horizontal(g19)
    c: PointOnObject(g16,g-3)
    c: PointOnObject(g17,g-5)
    c: PointOnObject(g13,g-5)
    c: DistanceX(g18,g-4) = 1.5
    c: DistanceX(g14,g16) = 1
    c: DistanceX(g16,g18) = 0.5
    c: DistanceX(g12,g14) = 0.5
    c: DistanceX(g10,g12) = 1
    c: DistanceX(g8,g10) = 0.5
    c: DistanceX(g6,g8) = 1
    c: DistanceX(g4,g6) = 0.5
    c: DistanceX(g2,g4) = 1
    c: DistanceX(g0,g2) = 0.5
    c: DistanceX(g-6,g0) = 2.2
FEATURE [PartDesign::Pocket] Pocket051
  BaseFeature = -> Pad219
  Direction = (0,1,-2e-16)
  Length = 0.5
  Length2 = 5
  Profile = -> Sketch334
  ReferenceAxis = -> Sketch334 [N_Axis]
  Refine = true
  Suppressed = false
  Type = 0
FEATURE [Sketcher::SketchObject] Sketch335
  ArcFitTolerance = 1e-06
  AttachmentSupport = -> [Pocket051]
  ExternalGeometry = -> [Pocket051]
  FullyConstrained = true
  MakeInternals = false
  MapMode = 5
  Placement = pos=(0,0,0) rot=(1,0,0;3.14159rad)
  sketch-geometry (12):
    g0: LineSegment StartX=1.5 StartY=-4.3 StartZ=0 EndX=1.5 EndY=-4.8 EndZ=0
    g1: LineSegment StartX=1.5 StartY=-4.8 StartZ=0 EndX=7.7 EndY=-4.8 EndZ=0
    g2: LineSegment StartX=7.7 StartY=-4.8 StartZ=0 EndX=7.7 EndY=-4.3 EndZ=0
    g3: LineSegment StartX=7.7 StartY=-4.3 StartZ=0 EndX=1.5 EndY=-4.3 EndZ=0
    g4: LineSegment StartX=1.5 StartY=-3.05 StartZ=0 EndX=1.5 EndY=-3.55 EndZ=0
    g5: LineSegment StartX=1.5 StartY=-3.55 StartZ=0 EndX=7.7 EndY=-3.55 EndZ=0
    g6: LineSegment StartX=7.7 StartY=-3.55 StartZ=0 EndX=7.7 EndY=-3.05 EndZ=0
    g7: LineSegment StartX=7.7 StartY=-3.05 StartZ=0 EndX=1.5 EndY=-3.05 EndZ=0
    g8: LineSegment StartX=1.5 StartY=-1.8 StartZ=0 EndX=1.5 EndY=-2.3 EndZ=0
    g9: LineSegment StartX=1.5 StartY=-2.3 StartZ=0 EndX=7.7 EndY=-2.3 EndZ=0
    g10: LineSegment StartX=7.7 StartY=-2.3 StartZ=0 EndX=7.7 EndY=-1.8 EndZ=0
    g11: LineSegment StartX=7.7 StartY=-1.8 StartZ=0 EndX=1.5 EndY=-1.8 EndZ=0
  constraints (37):
    c: Coincident(g0,g1)
    c: Coincident(g1,g2)
    c: Coincident(g2,g3)
    c: Coincident(g3,g0)
    c: Vertical(g0)
    c: Vertical(g2)
    c: Horizontal(g1)
    c: Horizontal(g3)
    c: Coincident(g4,g5)
    c: Coincident(g5,g6)
    c: Coincident(g6,g7)
    c: Coincident(g7,g4)
    c: Vertical(g4)
    c: Vertical(g6)
    c: Horizontal(g5)
    c: Horizontal(g7)
    c: Coincident(g8,g9)
    c: Coincident(g9,g10)
    c: Coincident(g10,g11)
    c: Coincident(g11,g8)
    c: Vertical(g8)
    c: Vertical(g10)
    c: Horizontal(g9)
    c: Horizontal(g11)
    c: DistanceY(g0,g0) = 0.5
    c: DistanceY(g4,g4) = 0.5
    c: DistanceY(g8,g8) = 0.5
    c: DistanceY(g0,g4) = 0.75
    c: DistanceY(g4,g8) = 0.75
    c: DistanceX(g-5,g0) = 1.5
    c: DistanceX(g3,g3) = 6.2
    c: DistanceX(g7,g7) = 6.2
    c: DistanceX(g1,g-4) = 2.5
    c: DistanceX(g11,g11) = 6.2
    c: DistanceX(g-5,g4) = 1.5
    c: DistanceX(g-5,g8) = 1.5
    c: DistanceY(g-5,g0) = 1.2
FEATURE [PartDesign::Pocket] Pocket052
  BaseFeature = -> Pocket051
  Direction = (0,0,1)
  Length = 0.5
  Length2 = 5
  Profile = -> Sketch335
  ReferenceAxis = -> Sketch335 [N_Axis]
  Refine = true
  Suppressed = false
  Type = 0
FEATURE [Sketcher::SketchObject] Sketch336
  ArcFitTolerance = 1e-06
  AttachmentSupport = -> [Pocket052]
  ExternalGeometry = -> [Pocket052]
  FullyConstrained = true
  MakeInternals = false
  MapMode = 5
  Placement = pos=(0,0,4) rot=(0,0,1;0rad)
  sketch-geometry (12):
    g0: LineSegment StartX=7.7 StartY=1.8 StartZ=0 EndX=7.7 EndY=2.3 EndZ=0
    g1: LineSegment StartX=7.7 StartY=2.3 StartZ=0 EndX=1.5 EndY=2.3 EndZ=0
    g2: LineSegment StartX=1.5 StartY=2.3 StartZ=0 EndX=1.5 EndY=1.8 EndZ=0
    g3: LineSegment StartX=1.5 StartY=1.8 StartZ=0 EndX=7.7 EndY=1.8 EndZ=0
    g4: LineSegment StartX=7.7 StartY=3.05 StartZ=0 EndX=7.7 EndY=3.55 EndZ=0
    g5: LineSegment StartX=7.7 StartY=3.55 StartZ=0 EndX=1.5 EndY=3.55 EndZ=0
    g6: LineSegment StartX=1.5 StartY=3.55 StartZ=0 EndX=1.5 EndY=3.05 EndZ=0
    g7: LineSegment StartX=1.5 StartY=3.05 StartZ=0 EndX=7.7 EndY=3.05 EndZ=0
    g8: LineSegment StartX=7.7 StartY=4.3 StartZ=0 EndX=7.7 EndY=4.8 EndZ=0
    g9: LineSegment StartX=7.7 StartY=4.8 StartZ=0 EndX=1.5 EndY=4.8 EndZ=0
    g10: LineSegment StartX=1.5 StartY=4.8 StartZ=0 EndX=1.5 EndY=4.3 EndZ=0
    g11: LineSegment StartX=1.5 StartY=4.3 StartZ=0 EndX=7.7 EndY=4.3 EndZ=0
  constraints (30):
    c: Coincident(g0,g1)
    c: Coincident(g1,g2)
    c: Coincident(g2,g3)
    c: Coincident(g3,g0)
    c: Vertical(g0)
    c: Vertical(g2)
    c: Horizontal(g1)
    c: Horizontal(g3)
    c: Coincident(g0,g-11)
    c: Coincident(g1,g-14)
    c: Coincident(g4,g5)
    c: Coincident(g5,g6)
    c: Coincident(g6,g7)
    c: Coincident(g7,g4)
    c: Vertical(g4)
    c: Vertical(g6)
    c: Horizontal(g5)
    c: Horizontal(g7)
    c: Coincident(g4,g-8)
    c: Coincident(g5,g-12)
    c: Coincident(g8,g9)
    c: Coincident(g9,g10)
    c: Coincident(g10,g11)
    c: Coincident(g11,g8)
    c: Vertical(g8)
    c: Vertical(g10)
    c: Horizontal(g9)
    c: Horizontal(g11)
    c: Coincident(g8,g-5)
    c: Coincident(g9,g-13)
FEATURE [PartDesign::Pocket] Pocket053
  BaseFeature = -> Pocket052
  Direction = (0,0,-1)
  Length = 0.5
  Length2 = 5
  Profile = -> Sketch336
  ReferenceAxis = -> Sketch336 [N_Axis]
  Refine = true
  Suppressed = false
  Type = 0
FEATURE [Sketcher::SketchObject] Sketch337
  ArcFitTolerance = 1e-06
  AttachmentSupport = -> [Pocket053]
  ExternalGeometry = -> [Pocket053]
  FullyConstrained = true
  MakeInternals = false
  MapMode = 5
  Placement = pos=(0,0,0) rot=(1,0,0;3.14159rad)
  sketch-geometry (8):
    g0: LineSegment StartX=1.5 StartY=-1.8 StartZ=0 EndX=7.7 EndY=-1.8 EndZ=0
    g1: LineSegment StartX=7.7 StartY=-1.8 StartZ=0 EndX=7.7 EndY=-6 EndZ=0
    g2: LineSegment StartX=7.7 StartY=-6 StartZ=0 EndX=8.7 EndY=-6 EndZ=0
    g3: LineSegment StartX=8.7 StartY=-6 StartZ=0 EndX=8.7 EndY=-1.1 EndZ=0
    g4: LineSegment StartX=8.2 StartY=-0.6 StartZ=0 EndX=1.5 EndY=-0.6 EndZ=0
    g5: LineSegment StartX=1.5 StartY=-0.6 StartZ=0 EndX=1.5 EndY=-1.8 EndZ=0
    g6: ArcOfCircle CenterX=8.2 CenterY=-1.1 CenterZ=0 NormalX=0 NormalY=0 NormalZ=1 AngleXU=0 Radius=0.5 StartAngle=1.65e-14 EndAngle=1.5708
    g7: GeomPoint [constr] X=8.7 Y=-0.6 Z=0
  constraints (20):
    c: Coincident(g0,g-3)
    c: Coincident(g0,g-5)
    c: Coincident(g1,g0)
    c: PointOnObject(g1,g-4)
    c: Vertical(g1)
    c: Coincident(g2,g1)
    c: PointOnObject(g2,g-4)
    c: Coincident(g3,g2)
    c: Vertical(g3)
    c: Horizontal(g4)
    c: Coincident(g5,g4)
    c: Coincident(g5,g0)
    c: Vertical(g5)
    c: DistanceY(g5,g5) = 1.2
    c: DistanceX(g2,g2) = 1
    c: PointOnObject(g7,g3)
    c: PointOnObject(g7,g4)
    c: Tangent(g3,g6) = -1.5708
    c: Tangent(g4,g6) = -1.5708
    c: Radius(g6) = 0.5
FEATURE [PartDesign::Pad] Pad220
  BaseFeature = -> Pocket053
  Direction = (0,0,-1)
  Length = 0.6
  Length2 = 10
  Profile = -> Sketch337
  ReferenceAxis = -> Sketch337 [N_Axis]
  Refine = true
  Suppressed = false
  Type = 0
FEATURE [Sketcher::SketchObject] Sketch338
  ArcFitTolerance = 1e-06
  AttachmentSupport = -> [Pad220]
  ExternalGeometry = -> [Pad220]
  FullyConstrained = true
  MakeInternals = false
  MapMode = 5
  Placement = pos=(0,0,4) rot=(0,0,1;0rad)
  sketch-geometry (7):
    g0: LineSegment StartX=8.7 StartY=1.1 StartZ=0 EndX=8.7 EndY=6 EndZ=0
    g1: LineSegment StartX=8.7 StartY=6 StartZ=0 EndX=7.7 EndY=6 EndZ=0
    g2: LineSegment StartX=7.7 StartY=6 StartZ=0 EndX=7.7 EndY=1.8 EndZ=0
    g3: LineSegment StartX=7.7 StartY=1.8 StartZ=0 EndX=1.5 EndY=1.8 EndZ=0
    g4: LineSegment StartX=1.5 StartY=1.8 StartZ=0 EndX=1.5 EndY=0.6 EndZ=0
    g5: LineSegment StartX=1.5 StartY=0.6 StartZ=0 EndX=8.2 EndY=0.6 EndZ=0
    g6: ArcOfCircle CenterX=8.20001 CenterY=1.09999 CenterZ=0 NormalX=0 NormalY=0 NormalZ=1 AngleXU=0 Radius=0.499993 StartAngle=4.71238 EndAngle=6.2832
  constraints (15):
    c: Coincident(g0,g-7)
    c: Coincident(g0,g-4)
    c: Coincident(g1,g0)
    c: Coincident(g1,g-5)
    c: Coincident(g2,g1)
    c: Coincident(g2,g-6)
    c: Coincident(g3,g2)
    c: Coincident(g3,g-9)
    c: Coincident(g4,g3)
    c: Coincident(g4,g-9)
    c: Coincident(g5,g4)
    c: Coincident(g5,g-8)
    c: Coincident(g6,g5)
    c: Coincident(g6,g0)
    c: Tangent(g6,g-7)
FEATURE [PartDesign::Pad] Pad221
  BaseFeature = -> Pad220
  Direction = (0,0,1)
  Length = 0.6
  Length2 = 10
  Profile = -> Sketch338
  ReferenceAxis = -> Sketch338 [N_Axis]
  Refine = true
  Suppressed = false
  Type = 0
FEATURE [Sketcher::SketchObject] Sketch339
  ArcFitTolerance = 1e-06
  AttachmentSupport = -> [Pad221]
  ExternalGeometry = -> [Pad221]
  FullyConstrained = true
  MakeInternals = false
  MapMode = 5
  Placement = pos=(10.2,0,0) rot=(0.57735,0.57735,0.57735;2.0944rad)
  sketch-geometry (4):
    g0: ArcOfCircle CenterX=3.9 CenterY=2 CenterZ=0 NormalX=0 NormalY=0 NormalZ=1 AngleXU=0 Radius=1.5 StartAngle=4.71239 EndAngle=7.85398
    g1: LineSegment StartX=3.9 StartY=3.5 StartZ=0 EndX=0.6 EndY=3.05 EndZ=0
    g2: LineSegment StartX=3.9 StartY=0.5 StartZ=0 EndX=0.6 EndY=0.95 EndZ=0
    g3: LineSegment StartX=0.6 StartY=0.95 StartZ=0 EndX=0.6 EndY=3.05 EndZ=0
  constraints (14):
    c: Coincident(g1,g0)
    c: Coincident(g2,g0)
    c: Coincident(g3,g2)
    c: Coincident(g3,g1)
    c: Vertical(g3)
    c: Diameter(g0) = 3
    c: DistanceY(g-3,g-3) = 4
    c: DistanceY(g0,g-4) = 2
    c: DistanceY(g3,g3) = 2.1
    c: DistanceY(g1,g-5) = 0.95
    c: DistanceX(g0,g0) = 0
    c: DistanceX(g0,g0) = 0
    c: DistanceX(g-5,g1) = 0.6
    c: DistanceX(g0,g-4) = 2.1
FEATURE [PartDesign::Pad] Pad222
  BaseFeature = -> Pad221
  Direction = (1,0,0)
  Length = 5
  Length2 = 10
  Profile = -> Sketch339
  ReferenceAxis = -> Sketch339 [N_Axis]
  Refine = true
  Suppressed = false
  Type = 0
FEATURE [Sketcher::SketchObject] Sketch340
  ArcFitTolerance = 1e-06
  AttachmentSupport = -> [Pad222]
  ExternalGeometry = -> [Pad222]
  FullyConstrained = true
  MakeInternals = false
  MapMode = 5
  Placement = pos=(0,0,0) rot=(1,0,0;3.14159rad)
  sketch-geometry (3):
    g0: LineSegment StartX=15.2 StartY=-0.6 StartZ=0 EndX=12.9 EndY=-0.6 EndZ=0
    g1: LineSegment StartX=15.2 StartY=-0.6 StartZ=0 EndX=15.2 EndY=-2.9 EndZ=0
    g2: LineSegment StartX=15.2 StartY=-2.9 StartZ=0 EndX=12.9 EndY=-0.6 EndZ=0
  constraints (8):
    c: Coincident(g0,g-4)
    c: PointOnObject(g0,g-4)
    c: Coincident(g1,g0)
    c: PointOnObject(g1,g-3)
    c: Coincident(g2,g1)
    c: Coincident(g2,g0)
    c: Angle(g1,g2) = 0.785398
    c: DistanceX(g0,g0) = 2.3
FEATURE [PartDesign::Pocket] Pocket054
  BaseFeature = -> Pad222
  Direction = (0,0,1)
  Length = 5
  Length2 = 5
  Profile = -> Sketch340
  ReferenceAxis = -> Sketch340 [N_Axis]
  Refine = true
  Suppressed = false
  Type = 0
FEATURE [Sketcher::SketchObject] Sketch341
  ArcFitTolerance = 1e-06
  AttachmentSupport = -> [Pocket054]
  ExternalGeometry = -> [Pocket054]
  FullyConstrained = true
  MakeInternals = false
  MapMode = 5
  Placement = pos=(0,0.138134,1.01298) rot=(1,0,0;3.00606rad)
  sketch-geometry (4):
    g0: LineSegment StartX=10.2 StartY=-1.26614 StartZ=0 EndX=10.2 EndY=-1.86614 EndZ=0
    g1: LineSegment StartX=10.2 StartY=-1.86614 StartZ=0 EndX=13 EndY=-1.86614 EndZ=0
    g2: LineSegment StartX=13 StartY=-1.86614 StartZ=0 EndX=13 EndY=-1.26614 EndZ=0
    g3: LineSegment StartX=13 StartY=-1.26614 StartZ=0 EndX=10.2 EndY=-1.26614 EndZ=0
  constraints (12):
    c: Coincident(g0,g1)
    c: Coincident(g1,g2)
    c: Coincident(g2,g3)
    c: Coincident(g3,g0)
    c: Vertical(g0)
    c: Vertical(g2)
    c: Horizontal(g1)
    c: Horizontal(g3)
    c: PointOnObject(g0,g-3)
    c: DistanceY(g2,g2) = 0.6
    c: DistanceX(g3,g3) = 2.8
    c: DistanceY(g0,g-4) = 0.8
FEATURE [PartDesign::Pocket] Pocket055
  BaseFeature = -> Pocket054
  Direction = (0,0.135113,0.99083)
  Length = 0.5
  Length2 = 5
  Profile = -> Sketch341
  ReferenceAxis = -> Sketch341 [N_Axis]
  Refine = true
  Suppressed = false
  Type = 0
FEATURE [Sketcher::SketchObject] Sketch342
  ArcFitTolerance = 1e-06
  AttachmentSupport = -> [Pocket055]
  ExternalGeometry = -> [Pocket055]
  FullyConstrained = true
  MakeInternals = false
  MapMode = 5
  Placement = pos=(0,-0.397363,2.914) rot=(1,0,0;0.135528rad)
  sketch-geometry (4):
    g0: LineSegment StartX=10.2 StartY=2.40659 StartZ=0 EndX=10.2 EndY=1.80659 EndZ=0
    g1: LineSegment StartX=10.2 StartY=1.80659 StartZ=0 EndX=13 EndY=1.80659 EndZ=0
    g2: LineSegment StartX=13 StartY=1.80659 StartZ=0 EndX=13 EndY=2.40659 EndZ=0
    g3: LineSegment StartX=13 StartY=2.40659 StartZ=0 EndX=10.2 EndY=2.40659 EndZ=0
  constraints (12):
    c: Coincident(g0,g1)
    c: Coincident(g1,g2)
    c: Coincident(g2,g3)
    c: Coincident(g3,g0)
    c: Vertical(g0)
    c: Vertical(g2)
    c: Horizontal(g1)
    c: Horizontal(g3)
    c: PointOnObject(g0,g-3)
    c: DistanceX(g1,g1) = 2.8
    c: DistanceY(g-4,g0) = 0.8
    c: DistanceY(g1,g2) = 0.6
FEATURE [PartDesign::Pocket] Pocket056
  BaseFeature = -> Pocket055
  Direction = (0,0.135113,-0.99083)
  Length = 0.5
  Length2 = 5
  Profile = -> Sketch342
  ReferenceAxis = -> Sketch342 [N_Axis]
  Refine = true
  Suppressed = false
  Type = 0
FEATURE [Sketcher::SketchObject] Sketch343
  ArcFitTolerance = 1e-06
  AttachmentSupport = -> [Pocket056]
  ExternalGeometry = -> [Pocket056]
  FullyConstrained = true
  MakeInternals = false
  MapMode = 5
  Placement = pos=(15.2,0,0) rot=(0.57735,0.57735,0.57735;2.0944rad)
  sketch-geometry (1):
    g0: Circle CenterX=3.9 CenterY=2 CenterZ=0 NormalX=0 NormalY=0 NormalZ=1 AngleXU=0 Radius=0.9
  constraints (2):
    c: Coincident(g0,g-3)
    c: Diameter(g0) = 1.8
FEATURE [PartDesign::Pad] Pad223
  BaseFeature = -> Pocket056
  Direction = (1,0,0)
  Length = 2.3
  Length2 = 10
  Profile = -> Sketch343
  ReferenceAxis = -> Sketch343 [N_Axis]
  Refine = true
  Suppressed = false
  Type = 0
FEATURE [Sketcher::SketchObject] Sketch344
  ArcFitTolerance = 1e-06
  AttachmentSupport = -> [Pad223]
  ExternalGeometry = -> [Pad223]
  FullyConstrained = true
  MakeInternals = false
  MapMode = 5
  Placement = pos=(17.5,0,0) rot=(0.57735,0.57735,0.57735;2.0944rad)
  sketch-geometry (1):
    g0: Circle CenterX=3.9 CenterY=2 CenterZ=0 NormalX=0 NormalY=0 NormalZ=1 AngleXU=0 Radius=1.25
  constraints (2):
    c: Coincident(g0,g-3)
    c: Diameter(g0) = 2.5
FEATURE [Sketcher::SketchObject] Sketch345
  ArcFitTolerance = 1e-06
  AttachmentOffset = pos=(0,0,4.4) rot=(0,0,1;0rad)
  AttachmentSupport = -> [Pad223]
  ExternalGeometry = -> [Pad223]
  FullyConstrained = true
  MakeInternals = false
  MapMode = 5
  Placement = pos=(21.9,0,0) rot=(0.57735,0.57735,0.57735;2.0944rad)
  sketch-geometry (1):
    g0: Circle CenterX=3.9 CenterY=2 CenterZ=0 NormalX=0 NormalY=0 NormalZ=1 AngleXU=0 Radius=1
  constraints (2):
    c: Coincident(g0,g-3)
    c: Diameter(g0) = 2
FEATURE [PartDesign::AdditiveLoft] AdditiveLoft020
  BaseFeature = -> Pad223
  Closed = false
  Profile = -> Sketch344
  Refine = true
  Ruled = false
  Sections = -> [Sketch345]
  Suppressed = false
FEATURE [Sketcher::SketchObject] Sketch346
  ArcFitTolerance = 1e-06
  AttachmentOffset = pos=(0,0,-0.75) rot=(0,0,1;0rad)
  AttachmentSupport = -> [AdditiveLoft020]
  ExternalGeometry = -> [AdditiveLoft020]
  FullyConstrained = true
  MakeInternals = false
  MapMode = 5
  Placement = pos=(0,0,0.75) rot=(1,0,0;3.14159rad)
  sketch-geometry (4):
    g0: LineSegment StartX=9.4 StartY=-6 StartZ=0 EndX=4.4 EndY=-6 EndZ=0
    g1: LineSegment StartX=4.4 StartY=-6 StartZ=0 EndX=4.4 EndY=-11.4 EndZ=0
    g2: LineSegment StartX=4.4 StartY=-11.4 StartZ=0 EndX=7.6 EndY=-11.4 EndZ=0
    g3: LineSegment StartX=7.6 StartY=-11.4 StartZ=0 EndX=9.4 EndY=-6 EndZ=0
  constraints (12):
    c: PointOnObject(g0,g-4)
    c: Coincident(g1,g0)
    c: Coincident(g2,g1)
    c: Horizontal(g2)
    c: Coincident(g3,g2)
    c: Coincident(g3,g0)
    c: DistanceX(g0,g0) = 5
    c: DistanceX(g2,g2) = 3.2
    c: Vertical(g1)
    c: DistanceY(g1,g0) = 5.4
    c: PointOnObject(g0,g-3)
    c: DistanceX(g0,g-3) = 0.8
FEATURE [PartDesign::Pad] Pad224
  BaseFeature = -> AdditiveLoft020
  Direction = (0,0,-1)
  Length = 2.5
  Length2 = 10
  Profile = -> Sketch346
  ReferenceAxis = -> Sketch346 [N_Axis]
  Refine = true
  Reversed = true
  Suppressed = false
  Type = 0
FEATURE [Sketcher::SketchObject] Sketch347
  ArcFitTolerance = 1e-06
  AttachmentSupport = -> [Pad224]
  ExternalGeometry = -> [Pad224]
  FullyConstrained = true
  MakeInternals = false
  MapMode = 5
  Placement = pos=(0,0,0) rot=(1,0,0;3.14159rad)
  sketch-geometry (6):
    g0: LineSegment StartX=0 StartY=-2.7 StartZ=0 EndX=-7.9 EndY=-2.7 EndZ=0
    g1: LineSegment StartX=-7.9 StartY=-2.7 StartZ=0 EndX=-7.9 EndY=-4 EndZ=0
    g2: LineSegment StartX=-7.9 StartY=-4 StartZ=0 EndX=-5.9 EndY=-6 EndZ=0
    g3: LineSegment StartX=-5.9 StartY=-6 StartZ=0 EndX=-5.9 EndY=-4.5 EndZ=0
    g4: LineSegment StartX=-5.9 StartY=-4.5 StartZ=0 EndX=0 EndY=-4.5 EndZ=0
    g5: LineSegment StartX=0 StartY=-4.5 StartZ=0 EndX=0 EndY=-2.7 EndZ=0
  constraints (18):
    c: PointOnObject(g0,g-3)
    c: Horizontal(g0)
    c: Coincident(g1,g0)
    c: Vertical(g1)
    c: Coincident(g2,g1)
    c: Coincident(g3,g2)
    c: Vertical(g3)
    c: Coincident(g4,g3)
    c: PointOnObject(g4,g-3)
    c: Horizontal(g4)
    c: Coincident(g5,g4)
    c: Coincident(g5,g0)
    c: DistanceX(g0,g0) = 7.9
    c: DistanceY(g-3,g2) = 0
    c: Angle(g2,g1) = 2.35619
    c: DistanceY(g3,g3) = 1.5
    c: DistanceY(g3,g0) = 1.8
    c: DistanceX(g4,g4) = 5.9
FEATURE [PartDesign::Pad] Pad225
  BaseFeature = -> Pad224
  Direction = (0,0,-1)
  Length = 4
  Length2 = 10
  Profile = -> Sketch347
  ReferenceAxis = -> Sketch347 [N_Axis]
  Refine = true
  Reversed = true
  Suppressed = false
  Type = 0
FEATURE [Sketcher::SketchObject] Sketch348
  ArcFitTolerance = 1e-06
  AttachmentOffset = pos=(0,0,-0.55) rot=(0,0,1;0rad)
  AttachmentSupport = -> [Pad225]
  ExternalGeometry = -> [Pad225]
  FullyConstrained = true
  MakeInternals = false
  MapMode = 5
  Placement = pos=(0,0,0.55) rot=(1,0,0;3.14159rad)
  sketch-geometry (4):
    g0: LineSegment StartX=-5.9 StartY=-4.5 StartZ=0 EndX=-5.9 EndY=-6 EndZ=0
    g1: LineSegment StartX=-5.9 StartY=-6 StartZ=0 EndX=0 EndY=-6 EndZ=0
    g2: LineSegment StartX=0 StartY=-6 StartZ=0 EndX=0 EndY=-4.5 EndZ=0
    g3: LineSegment StartX=0 StartY=-4.5 StartZ=0 EndX=-5.9 EndY=-4.5 EndZ=0
  constraints (10):
    c: Coincident(g0,g1)
    c: Coincident(g1,g2)
    c: Coincident(g2,g3)
    c: Coincident(g3,g0)
    c: Vertical(g0)
    c: Vertical(g2)
    c: Horizontal(g1)
    c: Horizontal(g3)
    c: Coincident(g0,g-5)
    c: Coincident(g1,g-3)
FEATURE [PartDesign::Pad] Pad226
  BaseFeature = -> Pad225
  Direction = (0,0,-1)
  Length = 2.9
  Length2 = 10
  Profile = -> Sketch348
  ReferenceAxis = -> Sketch348 [N_Axis]
  Refine = true
  Reversed = true
  Suppressed = false
  Type = 0
FEATURE [Sketcher::SketchObject] Sketch349
  ArcFitTolerance = 1e-06
  AttachmentSupport = -> [Pad226]
  ExternalGeometry = -> [Pad226]
  FullyConstrained = true
  MakeInternals = false
  MapMode = 5
  Placement = pos=(0,6,0) rot=(0,0.707107,0.707107;3.14159rad)
  sketch-geometry (1):
    g0: Circle CenterX=2.95 CenterY=2 CenterZ=0 NormalX=0 NormalY=0 NormalZ=1 AngleXU=0 Radius=1.7
  constraints (5):
    c: Radius(g0) = 1.7
    c: DistanceX(g-3,g-3) = 5.9
    c: DistanceX(g-3,g0) = 2.95
    c: DistanceY(g-5,g-5) = 2.9
    c: DistanceY(g0,g-3) = 1.45
FEATURE [PartDesign::Pad] Pad227
  BaseFeature = -> Pad226
  Direction = (0,1,-2e-16)
  Length = 2
  Length2 = 10
  Profile = -> Sketch349
  ReferenceAxis = -> Sketch349 [N_Axis]
  Refine = true
  Suppressed = false
  Type = 0
FEATURE [PartDesign::Pad] Pad228
  BaseFeature = -> Pad227
  Direction = (0,1,-2e-16)
  Length = 1.5
  Length2 = 10
  Profile = -> Sketch349
  ReferenceAxis = -> Sketch349 [N_Axis]
  Refine = true
  Reversed = true
  Suppressed = false
  Type = 0
FEATURE [Sketcher::SketchObject] Sketch350
  ArcFitTolerance = 1e-06
  AttachmentSupport = -> [Pad228]
  ExternalGeometry = -> [Pad228]
  FullyConstrained = true
  MakeInternals = false
  MapMode = 5
  Placement = pos=(0,8,-2.4e-15) rot=(0,0.707107,0.707107;3.14159rad)
  sketch-geometry (1):
    g0: Circle CenterX=2.95 CenterY=2 CenterZ=0 NormalX=0 NormalY=0 NormalZ=1 AngleXU=0 Radius=1.4
  constraints (2):
    c: Coincident(g0,g-3)
    c: Radius(g0) = 1.4
FEATURE [PartDesign::Pad] Pad229
  BaseFeature = -> Pad228
  Direction = (0,1,-2e-16)
  Length = 3.1
  Length2 = 10
  Profile = -> Sketch350
  ReferenceAxis = -> Sketch350 [N_Axis]
  Refine = true
  Suppressed = false
  Type = 0
FEATURE [PartDesign::Fillet] Fillet044
  Base = -> Pad229 [Edge279]
  BaseFeature = -> Pad229
  Radius = 1
  Refine = true
  SupportTransform = false
  Suppressed = false
  UseAllEdges = false
FEATURE [Sketcher::SketchObject] Sketch351
  ArcFitTolerance = 1e-06
  AttachmentOffset = pos=(0,0,-1.05) rot=(0,0,1;0rad)
  AttachmentSupport = -> [Fillet044]
  ExternalGeometry = -> [Fillet044]
  FullyConstrained = true
  MakeInternals = false
  MapMode = 5
  Placement = pos=(0,0,2.95) rot=(0,0,1;0rad)
  sketch-geometry (6):
    g0: LineSegment StartX=0 StartY=1 StartZ=0 EndX=0 EndY=2.7 EndZ=0
    g1: LineSegment StartX=0 StartY=2.7 StartZ=0 EndX=-6.7 EndY=2.7 EndZ=0
    g2: LineSegment StartX=-6.7 StartY=2.7 StartZ=0 EndX=-6 EndY=-2.45 EndZ=0
    g3: LineSegment StartX=-6 StartY=-2.45 StartZ=0 EndX=-3 EndY=-2.45 EndZ=0
    g4: LineSegment StartX=-3 StartY=-2.45 StartZ=0 EndX=-3 EndY=1 EndZ=0
    g5: LineSegment StartX=-3 StartY=1 StartZ=0 EndX=0 EndY=1 EndZ=0
  constraints (17):
    c: PointOnObject(g0,g-4)
    c: Coincident(g0,g-4)
    c: Coincident(g1,g0)
    c: PointOnObject(g1,g-3)
    c: Coincident(g2,g1)
    c: Coincident(g3,g2)
    c: Horizontal(g3)
    c: Coincident(g4,g3)
    c: Vertical(g4)
    c: Coincident(g5,g4)
    c: Coincident(g5,g0)
    c: Horizontal(g5)
    c: DistanceY(g2,g1) = 5.15
    c: DistanceX(g-3,g1) = 1.2
    c: DistanceX(g5,g5) = 3
    c: DistanceX(g3,g3) = 3
    c: DistanceY(g-1,g0) = 1
FEATURE [PartDesign::Pad] Pad230
  BaseFeature = -> Fillet044
  Direction = (0,0,1)
  Length = 1.9
  Length2 = 10
  Profile = -> Sketch351
  ReferenceAxis = -> Sketch351 [N_Axis]
  Refine = true
  Reversed = true
  Suppressed = false
  Type = 0
FEATURE [Sketcher::SketchObject] Sketch352
  ArcFitTolerance = 1e-06
  AttachmentSupport = -> [Pad230]
  ExternalGeometry = -> [Pad230]
  FullyConstrained = true
  MakeInternals = false
  MapMode = 5
  Placement = pos=(-7.9,0,0) rot=(0.57735,-0.57735,-0.57735;2.0944rad)
  sketch-geometry (6):
    g0: LineSegment StartX=-2.7 StartY=2.95 StartZ=0 EndX=2.45 EndY=2.75 EndZ=0
    g1: LineSegment StartX=2.45 StartY=2.75 StartZ=0 EndX=2.45 EndY=2.95 EndZ=0
    g2: LineSegment StartX=2.45 StartY=2.95 StartZ=0 EndX=-2.7 EndY=2.95 EndZ=0
    g3: LineSegment StartX=2.45 StartY=1.25 StartZ=0 EndX=2.45 EndY=1.05 EndZ=0
    g4: LineSegment StartX=2.45 StartY=1.25 StartZ=0 EndX=-2.7 EndY=1.05 EndZ=0
    g5: LineSegment StartX=-2.7 StartY=1.05 StartZ=0 EndX=2.45 EndY=1.05 EndZ=0
  constraints (15):
    c: Coincident(g0,g-4)
    c: PointOnObject(g0,g-3)
    c: Coincident(g1,g0)
    c: Coincident(g1,g-4)
    c: Coincident(g2,g1)
    c: Coincident(g2,g0)
    c: PointOnObject(g3,g-3)
    c: Coincident(g3,g-5)
    c: Coincident(g4,g3)
    c: Coincident(g4,g-5)
    c: Coincident(g5,g4)
    c: Coincident(g5,g3)
    c: DistanceY(g3,g0) = 1.5
    c: DistanceY(g3,g1) = 1.9
    c: DistanceY(g0,g1) = 0.2
FEATURE [PartDesign::Pocket] Pocket057
  BaseFeature = -> Pad230
  Direction = (1,0,0)
  Length = 7.9
  Length2 = 5
  Profile = -> Sketch352
  ReferenceAxis = -> Sketch352 [N_Axis]
  Refine = true
  Suppressed = false
  Type = 0
FEATURE [Sketcher::SketchObject] Sketch353
  ArcFitTolerance = 1e-06
  AttachmentSupport = -> [Pocket057]
  ExternalGeometry = -> [Pocket057]
  FullyConstrained = true
  MakeInternals = false
  MapMode = 5
  Placement = pos=(-3,0,0) rot=(0.57735,0.57735,0.57735;2.0944rad)
  sketch-geometry (1):
    g0: Circle CenterX=-2.45 CenterY=2 CenterZ=0 NormalX=0 NormalY=0 NormalZ=1 AngleXU=0 Radius=1.5
  constraints (2):
    c: Symmetric(g-3,g-3,g0)
    c: Diameter(g0) = 3
FEATURE [PartDesign::Pad] Pad231
  BaseFeature = -> Pocket057
  Direction = (1,0,0)
  Length = 7
  Length2 = 10
  Profile = -> Sketch353
  ReferenceAxis = -> Sketch353 [N_Axis]
  Refine = true
  Suppressed = false
  Type = 0
FEATURE [PartDesign::Body] Body024  label="Hook_Gun"
  AllowCompound = false
  Group = -> [Sketch333,Pad219,Sketch334,Pocket051,Sketch335,Pocket052,Sketch336,Pocket053,Sketch337,Pad220,Sketch338,Pad221,Sketch339,Pad222,Sketch340,Pocket054,Sketch341,Pocket055,Sketch342,Pocket056,Sketch343,Pad223,Sketch344,Sketch345,AdditiveLoft020,Sketch346,Pad224,Sketch347,Pad225,Sketch348,Pad226,Sketch349,Pad227,Pad228,Sketch350,Pad229,Fillet044,Sketch351,Pad230,Sketch352,Pocket057,Sketch353,Pad231,+8 more]
  Origin = -> Origin026
  Placement = pos=(-3.05,-5,-29.9) rot=(1,0,0;4.71239rad)
  Tip = -> Pocket059
